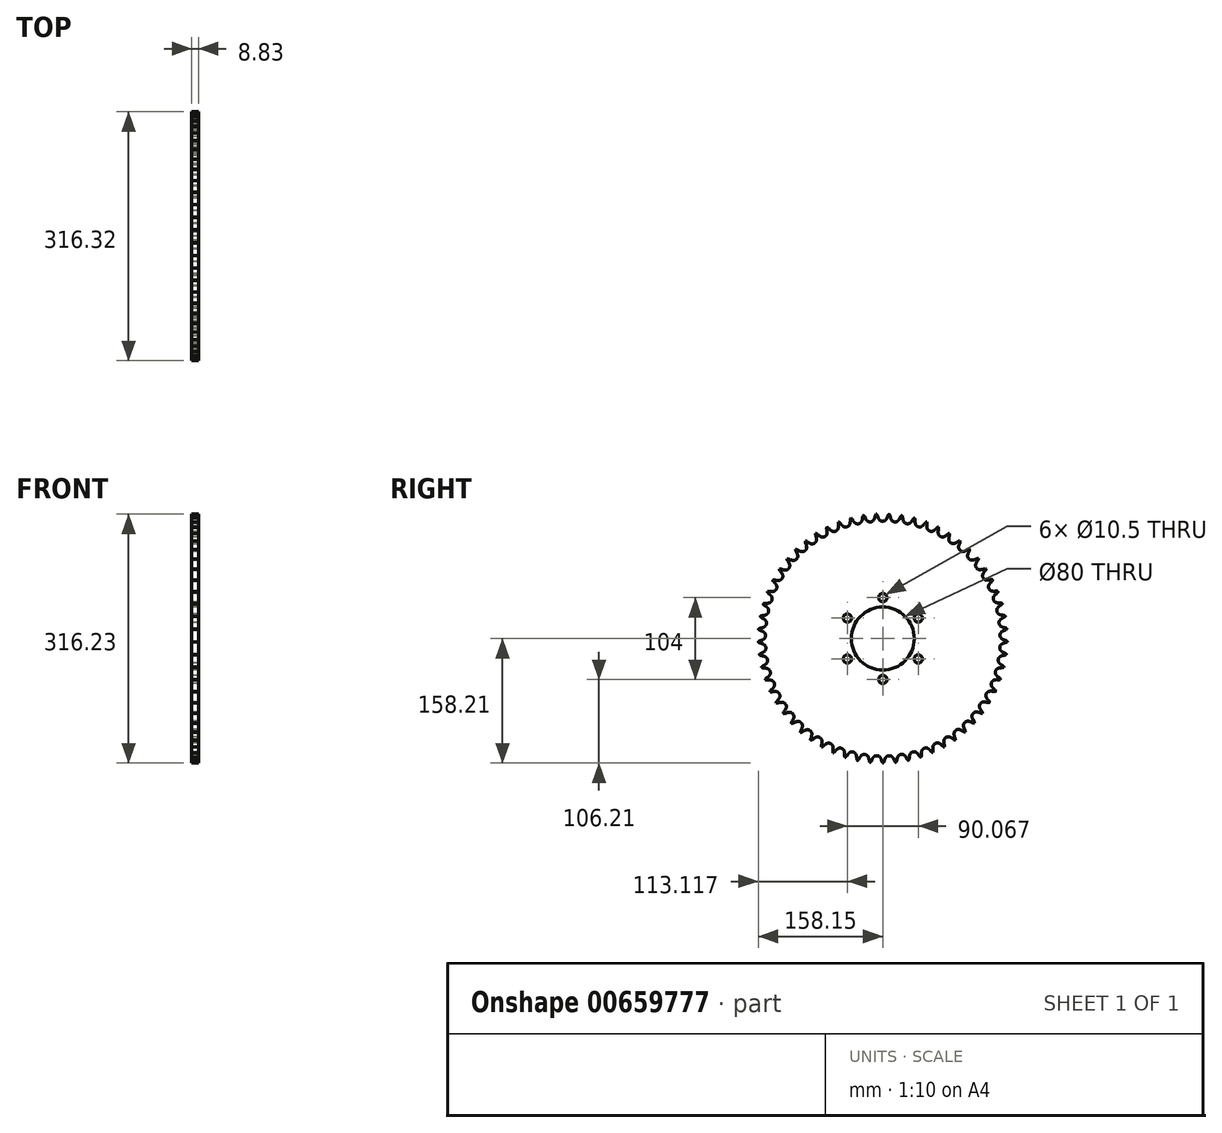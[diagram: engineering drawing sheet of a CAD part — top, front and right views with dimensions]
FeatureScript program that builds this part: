
annotation { "Feature Type Name" : "Feature", "Feature Type Description" : "" }
export const myFeature = defineFeature(function(context is Context, id is Id, definition is map)
    precondition{}
    {
        {
            var Q0;
            Q0=qCreatedBy(makeId("Front.planeOp"),FACE);
            var sketch = newSketch(context, id + "F0", { "sketchPlane" : qUnion([Q0])});
            skLineSegment(sketch, "E0", {"start": v(0, 0) * mm, "end": v(26.72, 0) * mm, "construction": true});
            skLineSegment(sketch, "E1.bottom", {"start": v(0, 40) * mm, "end": v(8.83, 40) * mm});
            skLineSegment(sketch, "E1.top", {"start": v(0, 158.2) * mm, "end": v(8.83, 158.2) * mm});
            skLineSegment(sketch, "E1.left", {"start": v(0, 40) * mm, "end": v(0, 158.2) * mm});
            skLineSegment(sketch, "E1.right", {"start": v(8.83, 40) * mm, "end": v(8.82, 158.2) * mm});
            skLineSegment(sketch, "E2.MirrorCS", {"start": v(8.83, -40) * mm, "end": v(8.83, -158.2) * mm});
            skLineSegment(sketch, "E3.MirrorCS", {"start": v(0, -158.2) * mm, "end": v(8.83, -158.2) * mm});
            skLineSegment(sketch, "E4.MirrorCS", {"start": v(0, -40) * mm, "end": v(8.83, -40) * mm});
            skLineSegment(sketch, "E5.MirrorCS", {"start": v(0, -40) * mm, "end": v(0, -158.2) * mm});
            skSolve(sketch);
        }
        {
            var Q0;
            Q0=makeQuery(id+"F0.imprint","IMPRINT",FACE,{"disambiguationData":[TD([[makeQuery(id+"F0.imprint","IMPRINT",EDGE,{"derivedFrom":sQuery(id+"F0.wireOp",EDGE,"E1.bottom")}),1.0]])]});
            var Q1;
            Q1=sQuery(id+"F0.wireOp",EDGE,"E0");
            revolve(context, id + "F1", {"entities" : qUnion([Q0]), "axis" : qUnion([Q1]), "revolveType" : RevolveType.FULL});
        }
        {
            var Q0;
            Q0=makeQuery(id+"F1.opRevolve","SWEPT_FACE",FACE,{"disambiguationData":[OSD([sQuery(id+"F0.wireOp",EDGE,"E1.left")])]});
            var sketch = newSketch(context, id + "F2", { "sketchPlane" : qUnion([Q0])});
            skCircle(sketch, "E6", {"center": v(0.24, 0) * mm, "radius": 158.2 * mm, "construction": true});
            skCircle(sketch, "E7", {"center": v(0.24, 0) * mm, "radius": 154.2 * mm, "construction": true});
            skCircle(sketch, "E8", {"center": v(0.24, 0) * mm, "radius": 149.03 * mm, "construction": true});
            skLineSegment(sketch, "E9", {"start": v(0.24, 0) * mm, "end": v(0.24, 107.73) * mm, "construction": true});
            skLineSegment(sketch, "E10", {"start": v(-4.24, 86.97) * mm, "end": v(0.24, 0) * mm, "construction": true});
            skLineSegment(sketch, "E11", {"start": v(0, 0) * mm, "end": v(0, 107.73) * mm, "construction": true});
            skLineSegment(sketch, "E12", {"start": v(0, 154.19) * mm, "end": v(-70.6, 102.92) * mm, "construction": true});
            skLineSegment(sketch, "E13", {"start": v(0, 154.19) * mm, "end": v(6.58, 158.97) * mm, "construction": true});
            skLineSegment(sketch, "E14", {"start": v(6.58, 158.97) * mm, "end": v(-48.08, 140.25) * mm, "construction": true});
            skLineSegment(sketch, "E15", {"start": v(-5.99, 154.66) * mm, "end": v(-6.34, 155.68) * mm});
            skLineSegment(sketch, "E16", {"start": v(-6.34, 155.68) * mm, "end": v(-12.58, 153.54) * mm, "construction": true});
            skArc(sketch, "E17", {"start": v(-5.99, 154.66) * mm, "mid": v(-5.21, 152.84) * mm, "end": v(-4.17, 151.16) * mm});
            skArc(sketch, "E18", {"start": v(-4.17, 151.16) * mm, "mid": v(18.37, 165.09) * mm, "end": v(-5.99, 154.66) * mm, "construction": true});
            skArc(sketch, "E19", {"start": v(0, 149.03) * mm, "mid": v(2.34, 158.78) * mm, "end": v(-4.17, 151.16) * mm, "construction": true});
            skArc(sketch, "E20", {"start": v(-4.17, 151.16) * mm, "mid": v(-2.34, 149.6) * mm, "end": v(0, 149.03) * mm});
            skLineSegment(sketch, "E21", {"start": v(0, 149.03) * mm, "end": v(0.24, 149.03) * mm});
            skArc(sketch, "E22", {"start": v(-7.92, 158.21) * mm, "mid": v(-18.18, 150.05) * mm, "end": v(-6.34, 155.68) * mm, "construction": true});
            skArc(sketch, "E23", {"start": v(-6.34, 155.68) * mm, "mid": v(-6.98, 157.04) * mm, "end": v(-7.92, 158.21) * mm});
            skArc(sketch, "E24.MirrorCS", {"start": v(4.65, 151.16) * mm, "mid": v(2.82, 149.6) * mm, "end": v(0.48, 149.03) * mm});
            skArc(sketch, "E25.MirrorCS", {"start": v(6.47, 154.66) * mm, "mid": v(5.69, 152.84) * mm, "end": v(4.65, 151.16) * mm});
            skLineSegment(sketch, "E26.MirrorCS", {"start": v(6.47, 154.66) * mm, "end": v(6.81, 155.68) * mm});
            skArc(sketch, "E27.MirrorCS", {"start": v(6.81, 155.68) * mm, "mid": v(7.46, 157.04) * mm, "end": v(8.4, 158.21) * mm});
            skLineSegment(sketch, "E28.MirrorCS", {"start": v(0.48, 149.03) * mm, "end": v(0.24, 149.03) * mm});
            skArc(sketch, "E29.1.0", {"start": v(-22.31, 154.2) * mm, "mid": v(-23.1, 155.49) * mm, "end": v(-24.14, 156.56) * mm});
            skArc(sketch, "E29.1.1", {"start": v(-9.23, 155.56) * mm, "mid": v(-8.73, 156.97) * mm, "end": v(-7.92, 158.23) * mm});
            skLineSegment(sketch, "E29.1.2", {"start": v(-9.47, 154.5) * mm, "end": v(-9.23, 155.56) * mm});
            skArc(sketch, "E29.1.3", {"start": v(-9.47, 154.5) * mm, "mid": v(-10.06, 152.62) * mm, "end": v(-10.92, 150.84) * mm});
            skArc(sketch, "E29.1.4", {"start": v(-10.92, 150.84) * mm, "mid": v(-12.58, 149.1) * mm, "end": v(-14.85, 148.3) * mm});
            skArc(sketch, "E29.1.5", {"start": v(-19.7, 149.93) * mm, "mid": v(-17.71, 148.56) * mm, "end": v(-15.32, 148.24) * mm});
            skArc(sketch, "E29.1.6", {"start": v(-21.86, 153.23) * mm, "mid": v(-20.9, 151.5) * mm, "end": v(-19.7, 149.93) * mm});
            skLineSegment(sketch, "E29.1.7", {"start": v(-21.86, 153.23) * mm, "end": v(-22.31, 154.2) * mm});
            skLineSegment(sketch, "E29.1.8", {"start": v(-14.85, 148.3) * mm, "end": v(-15.09, 148.27) * mm});
            skLineSegment(sketch, "E29.1.9", {"start": v(-15.32, 148.24) * mm, "end": v(-15.09, 148.27) * mm});
            skArc(sketch, "E29.2.0", {"start": v(-38.05, 151.1) * mm, "mid": v(-38.96, 152.29) * mm, "end": v(-40.11, 153.25) * mm});
            skArc(sketch, "E29.2.1", {"start": v(-25.17, 153.78) * mm, "mid": v(-24.82, 155.24) * mm, "end": v(-24.15, 156.58) * mm});
            skLineSegment(sketch, "E29.2.2", {"start": v(-25.3, 152.71) * mm, "end": v(-25.17, 153.78) * mm});
            skArc(sketch, "E29.2.3", {"start": v(-25.3, 152.71) * mm, "mid": v(-25.7, 150.78) * mm, "end": v(-26.37, 148.92) * mm});
            skArc(sketch, "E29.2.4", {"start": v(-26.37, 148.92) * mm, "mid": v(-27.84, 147.01) * mm, "end": v(-30.02, 145.98) * mm});
            skArc(sketch, "E29.2.5", {"start": v(-35, 147.11) * mm, "mid": v(-32.9, 145.96) * mm, "end": v(-30.49, 145.88) * mm});
            skArc(sketch, "E29.2.6", {"start": v(-37.5, 150.17) * mm, "mid": v(-36.37, 148.55) * mm, "end": v(-35, 147.11) * mm});
            skLineSegment(sketch, "E29.2.7", {"start": v(-37.5, 150.17) * mm, "end": v(-38.05, 151.1) * mm});
            skLineSegment(sketch, "E29.2.8", {"start": v(-30.02, 145.98) * mm, "end": v(-30.25, 145.93) * mm});
            skLineSegment(sketch, "E29.2.9", {"start": v(-30.49, 145.88) * mm, "end": v(-30.25, 145.93) * mm});
            skArc(sketch, "E29.3.0", {"start": v(-53.38, 146.38) * mm, "mid": v(-54.4, 147.47) * mm, "end": v(-55.66, 148.3) * mm});
            skArc(sketch, "E29.3.1", {"start": v(-40.85, 150.38) * mm, "mid": v(-40.65, 151.87) * mm, "end": v(-40.12, 153.27) * mm});
            skLineSegment(sketch, "E29.3.2", {"start": v(-40.88, 149.3) * mm, "end": v(-40.85, 150.38) * mm});
            skArc(sketch, "E29.3.3", {"start": v(-40.88, 149.3) * mm, "mid": v(-41.06, 147.33) * mm, "end": v(-41.54, 145.41) * mm});
            skArc(sketch, "E29.3.4", {"start": v(-41.54, 145.41) * mm, "mid": v(-42.81, 143.37) * mm, "end": v(-44.87, 142.12) * mm});
            skArc(sketch, "E29.3.5", {"start": v(-49.94, 142.73) * mm, "mid": v(-47.72, 141.8) * mm, "end": v(-45.32, 141.98) * mm});
            skArc(sketch, "E29.3.6", {"start": v(-52.74, 145.52) * mm, "mid": v(-51.45, 144.02) * mm, "end": v(-49.94, 142.73) * mm});
            skLineSegment(sketch, "E29.3.7", {"start": v(-52.74, 145.52) * mm, "end": v(-53.38, 146.38) * mm});
            skLineSegment(sketch, "E29.3.8", {"start": v(-44.87, 142.12) * mm, "end": v(-45.1, 142.05) * mm});
            skLineSegment(sketch, "E29.3.9", {"start": v(-45.32, 141.98) * mm, "end": v(-45.1, 142.05) * mm});
            skArc(sketch, "E29.4.0", {"start": v(-68.15, 140.11) * mm, "mid": v(-69.28, 141.1) * mm, "end": v(-70.61, 141.8) * mm});
            skArc(sketch, "E29.4.1", {"start": v(-56.1, 145.38) * mm, "mid": v(-56.05, 146.88) * mm, "end": v(-55.67, 148.33) * mm});
            skLineSegment(sketch, "E29.4.2", {"start": v(-56.01, 144.3) * mm, "end": v(-56.1, 145.38) * mm});
            skArc(sketch, "E29.4.3", {"start": v(-56.01, 144.3) * mm, "mid": v(-56, 142.33) * mm, "end": v(-56.27, 140.37) * mm});
            skArc(sketch, "E29.4.4", {"start": v(-56.27, 140.37) * mm, "mid": v(-57.33, 138.2) * mm, "end": v(-59.25, 136.75) * mm});
            skArc(sketch, "E29.4.5", {"start": v(-64.36, 136.84) * mm, "mid": v(-62.05, 136.14) * mm, "end": v(-59.68, 136.56) * mm});
            skArc(sketch, "E29.4.6", {"start": v(-67.42, 139.32) * mm, "mid": v(-65.98, 137.97) * mm, "end": v(-64.36, 136.84) * mm});
            skLineSegment(sketch, "E29.4.7", {"start": v(-67.42, 139.32) * mm, "end": v(-68.15, 140.11) * mm});
            skLineSegment(sketch, "E29.4.8", {"start": v(-59.25, 136.75) * mm, "end": v(-59.46, 136.66) * mm});
            skLineSegment(sketch, "E29.4.9", {"start": v(-59.68, 136.56) * mm, "end": v(-59.46, 136.66) * mm});
            skArc(sketch, "E29.5.0", {"start": v(-82.2, 132.36) * mm, "mid": v(-83.42, 133.23) * mm, "end": v(-84.82, 133.79) * mm});
            skArc(sketch, "E29.5.1", {"start": v(-70.75, 138.84) * mm, "mid": v(-70.86, 140.34) * mm, "end": v(-70.62, 141.82) * mm});
            skLineSegment(sketch, "E29.5.2", {"start": v(-70.55, 137.79) * mm, "end": v(-70.75, 138.84) * mm});
            skArc(sketch, "E29.5.3", {"start": v(-70.55, 137.79) * mm, "mid": v(-70.33, 135.82) * mm, "end": v(-70.4, 133.84) * mm});
            skArc(sketch, "E29.5.4", {"start": v(-70.4, 133.84) * mm, "mid": v(-71.23, 131.58) * mm, "end": v(-73, 129.94) * mm});
            skArc(sketch, "E29.5.5", {"start": v(-78.08, 129.5) * mm, "mid": v(-75.72, 129.04) * mm, "end": v(-73.4, 129.7) * mm});
            skArc(sketch, "E29.5.6", {"start": v(-81.4, 131.65) * mm, "mid": v(-79.82, 130.45) * mm, "end": v(-78.08, 129.5) * mm});
            skLineSegment(sketch, "E29.5.7", {"start": v(-81.4, 131.65) * mm, "end": v(-82.2, 132.36) * mm});
            skLineSegment(sketch, "E29.5.8", {"start": v(-73, 129.94) * mm, "end": v(-73.2, 129.82) * mm});
            skLineSegment(sketch, "E29.5.9", {"start": v(-73.4, 129.7) * mm, "end": v(-73.2, 129.82) * mm});
            skArc(sketch, "E29.6.0", {"start": v(-95.37, 123.21) * mm, "mid": v(-96.68, 123.94) * mm, "end": v(-98.12, 124.36) * mm});
            skArc(sketch, "E29.6.1", {"start": v(-84.65, 130.83) * mm, "mid": v(-84.91, 132.31) * mm, "end": v(-84.83, 133.8) * mm});
            skLineSegment(sketch, "E29.6.2", {"start": v(-84.35, 129.8) * mm, "end": v(-84.65, 130.83) * mm});
            skArc(sketch, "E29.6.3", {"start": v(-84.35, 129.8) * mm, "mid": v(-83.93, 127.87) * mm, "end": v(-83.8, 125.9) * mm});
            skArc(sketch, "E29.6.4", {"start": v(-83.8, 125.9) * mm, "mid": v(-84.38, 123.56) * mm, "end": v(-85.97, 121.74) * mm});
            skArc(sketch, "E29.6.5", {"start": v(-90.99, 120.78) * mm, "mid": v(-88.59, 120.57) * mm, "end": v(-86.35, 121.47) * mm});
            skArc(sketch, "E29.6.6", {"start": v(-94.5, 122.58) * mm, "mid": v(-92.8, 121.55) * mm, "end": v(-90.99, 120.78) * mm});
            skLineSegment(sketch, "E29.6.7", {"start": v(-94.5, 122.58) * mm, "end": v(-95.37, 123.21) * mm});
            skLineSegment(sketch, "E29.6.8", {"start": v(-85.97, 121.74) * mm, "end": v(-86.16, 121.6) * mm});
            skLineSegment(sketch, "E29.6.9", {"start": v(-86.35, 121.47) * mm, "end": v(-86.16, 121.6) * mm});
            skArc(sketch, "E29.7.0", {"start": v(-107.53, 112.75) * mm, "mid": v(-108.91, 113.34) * mm, "end": v(-110.39, 113.61) * mm});
            skArc(sketch, "E29.7.1", {"start": v(-97.65, 121.43) * mm, "mid": v(-98.06, 122.88) * mm, "end": v(-98.14, 124.38) * mm});
            skLineSegment(sketch, "E29.7.2", {"start": v(-97.24, 120.44) * mm, "end": v(-97.65, 121.43) * mm});
            skArc(sketch, "E29.7.3", {"start": v(-97.24, 120.44) * mm, "mid": v(-96.63, 118.56) * mm, "end": v(-96.3, 116.6) * mm});
            skArc(sketch, "E29.7.4", {"start": v(-96.3, 116.6) * mm, "mid": v(-96.64, 114.23) * mm, "end": v(-98.03, 112.26) * mm});
            skArc(sketch, "E29.7.5", {"start": v(-102.92, 110.79) * mm, "mid": v(-100.52, 110.82) * mm, "end": v(-98.39, 111.94) * mm});
            skArc(sketch, "E29.7.6", {"start": v(-106.6, 112.22) * mm, "mid": v(-104.81, 111.37) * mm, "end": v(-102.92, 110.79) * mm});
            skLineSegment(sketch, "E29.7.7", {"start": v(-106.6, 112.22) * mm, "end": v(-107.53, 112.75) * mm});
            skLineSegment(sketch, "E29.7.8", {"start": v(-98.03, 112.26) * mm, "end": v(-98.2, 112.1) * mm});
            skLineSegment(sketch, "E29.7.9", {"start": v(-98.39, 111.94) * mm, "end": v(-98.2, 112.1) * mm});
            skArc(sketch, "E29.8.0", {"start": v(-118.56, 101.1) * mm, "mid": v(-119.99, 101.55) * mm, "end": v(-121.49, 101.66) * mm});
            skArc(sketch, "E29.8.1", {"start": v(-109.62, 110.75) * mm, "mid": v(-110.18, 112.14) * mm, "end": v(-110.4, 113.63) * mm});
            skLineSegment(sketch, "E29.8.2", {"start": v(-109.11, 109.8) * mm, "end": v(-109.62, 110.75) * mm});
            skArc(sketch, "E29.8.3", {"start": v(-109.11, 109.8) * mm, "mid": v(-108.3, 108) * mm, "end": v(-107.78, 106.1) * mm});
            skArc(sketch, "E29.8.4", {"start": v(-107.78, 106.1) * mm, "mid": v(-107.87, 103.68) * mm, "end": v(-109.05, 101.58) * mm});
            skArc(sketch, "E29.8.5", {"start": v(-113.77, 99.62) * mm, "mid": v(-111.38, 99.9) * mm, "end": v(-109.37, 101.24) * mm});
            skArc(sketch, "E29.8.6", {"start": v(-117.57, 100.66) * mm, "mid": v(-115.7, 100) * mm, "end": v(-113.77, 99.62) * mm});
            skLineSegment(sketch, "E29.8.7", {"start": v(-117.57, 100.66) * mm, "end": v(-118.56, 101.1) * mm});
            skLineSegment(sketch, "E29.8.8", {"start": v(-109.05, 101.58) * mm, "end": v(-109.21, 101.41) * mm});
            skLineSegment(sketch, "E29.8.9", {"start": v(-109.37, 101.24) * mm, "end": v(-109.21, 101.41) * mm});
            skArc(sketch, "E29.9.0", {"start": v(-128.32, 88.37) * mm, "mid": v(-129.8, 88.67) * mm, "end": v(-131.3, 88.63) * mm});
            skArc(sketch, "E29.9.1", {"start": v(-120.43, 98.9) * mm, "mid": v(-121.13, 100.22) * mm, "end": v(-121.5, 101.67) * mm});
            skLineSegment(sketch, "E29.9.2", {"start": v(-119.82, 98) * mm, "end": v(-120.43, 98.9) * mm});
            skArc(sketch, "E29.9.3", {"start": v(-119.82, 98) * mm, "mid": v(-118.84, 96.29) * mm, "end": v(-118.12, 94.45) * mm});
            skArc(sketch, "E29.9.4", {"start": v(-118.12, 94.45) * mm, "mid": v(-117.96, 92.04) * mm, "end": v(-118.92, 89.83) * mm});
            skArc(sketch, "E29.9.5", {"start": v(-123.4, 87.4) * mm, "mid": v(-121.06, 87.92) * mm, "end": v(-119.2, 89.45) * mm});
            skArc(sketch, "E29.9.6", {"start": v(-127.3, 88.04) * mm, "mid": v(-125.38, 87.57) * mm, "end": v(-123.4, 87.4) * mm});
            skLineSegment(sketch, "E29.9.7", {"start": v(-127.3, 88.04) * mm, "end": v(-128.32, 88.37) * mm});
            skLineSegment(sketch, "E29.9.8", {"start": v(-118.92, 89.83) * mm, "end": v(-119.06, 89.64) * mm});
            skLineSegment(sketch, "E29.9.9", {"start": v(-119.2, 89.45) * mm, "end": v(-119.06, 89.64) * mm});
            skArc(sketch, "E29.10.0", {"start": v(-136.73, 74.7) * mm, "mid": v(-138.22, 74.85) * mm, "end": v(-139.71, 74.66) * mm});
            skArc(sketch, "E29.10.1", {"start": v(-129.96, 85.98) * mm, "mid": v(-130.79, 87.24) * mm, "end": v(-131.32, 88.64) * mm});
            skLineSegment(sketch, "E29.10.2", {"start": v(-129.27, 85.16) * mm, "end": v(-129.96, 85.98) * mm});
            skArc(sketch, "E29.10.3", {"start": v(-129.27, 85.16) * mm, "mid": v(-128.1, 83.56) * mm, "end": v(-127.2, 81.8) * mm});
            skArc(sketch, "E29.10.4", {"start": v(-127.2, 81.8) * mm, "mid": v(-126.8, 79.43) * mm, "end": v(-127.52, 77.13) * mm});
            skArc(sketch, "E29.10.5", {"start": v(-131.74, 74.24) * mm, "mid": v(-129.46, 75) * mm, "end": v(-127.77, 76.72) * mm});
            skArc(sketch, "E29.10.6", {"start": v(-135.68, 74.48) * mm, "mid": v(-133.72, 74.22) * mm, "end": v(-131.74, 74.24) * mm});
            skLineSegment(sketch, "E29.10.7", {"start": v(-135.68, 74.48) * mm, "end": v(-136.73, 74.7) * mm});
            skLineSegment(sketch, "E29.10.8", {"start": v(-127.52, 77.13) * mm, "end": v(-127.65, 76.93) * mm});
            skLineSegment(sketch, "E29.10.9", {"start": v(-127.77, 76.72) * mm, "end": v(-127.65, 76.93) * mm});
            skArc(sketch, "E29.11.0", {"start": v(-143.69, 60.25) * mm, "mid": v(-145.19, 60.25) * mm, "end": v(-146.65, 59.9) * mm});
            skArc(sketch, "E29.11.1", {"start": v(-138.11, 72.17) * mm, "mid": v(-139.07, 73.32) * mm, "end": v(-139.73, 74.67) * mm});
            skLineSegment(sketch, "E29.11.2", {"start": v(-137.34, 71.42) * mm, "end": v(-138.11, 72.17) * mm});
            skArc(sketch, "E29.11.3", {"start": v(-137.34, 71.42) * mm, "mid": v(-136.02, 69.94) * mm, "end": v(-134.94, 68.29) * mm});
            skArc(sketch, "E29.11.4", {"start": v(-134.94, 68.29) * mm, "mid": v(-134.3, 65.97) * mm, "end": v(-134.78, 63.6) * mm});
            skArc(sketch, "E29.11.5", {"start": v(-138.68, 60.3) * mm, "mid": v(-136.48, 61.3) * mm, "end": v(-134.98, 63.18) * mm});
            skArc(sketch, "E29.11.6", {"start": v(-142.62, 60.14) * mm, "mid": v(-140.64, 60.07) * mm, "end": v(-138.68, 60.3) * mm});
            skLineSegment(sketch, "E29.11.7", {"start": v(-142.62, 60.14) * mm, "end": v(-143.69, 60.25) * mm});
            skLineSegment(sketch, "E29.11.8", {"start": v(-134.78, 63.6) * mm, "end": v(-134.88, 63.4) * mm});
            skLineSegment(sketch, "E29.11.9", {"start": v(-134.98, 63.18) * mm, "end": v(-134.88, 63.4) * mm});
            skArc(sketch, "E29.12.0", {"start": v(-149.12, 45.16) * mm, "mid": v(-150.61, 45) * mm, "end": v(-152.03, 44.5) * mm});
            skArc(sketch, "E29.12.1", {"start": v(-144.8, 57.58) * mm, "mid": v(-145.87, 58.64) * mm, "end": v(-146.67, 59.9) * mm});
            skLineSegment(sketch, "E29.12.2", {"start": v(-143.95, 56.92) * mm, "end": v(-144.8, 57.58) * mm});
            skArc(sketch, "E29.12.3", {"start": v(-143.95, 56.92) * mm, "mid": v(-142.5, 55.59) * mm, "end": v(-141.24, 54.05) * mm});
            skArc(sketch, "E29.12.4", {"start": v(-141.24, 54.05) * mm, "mid": v(-140.37, 51.8) * mm, "end": v(-140.6, 49.41) * mm});
            skArc(sketch, "E29.12.5", {"start": v(-144.14, 45.72) * mm, "mid": v(-142.06, 46.94) * mm, "end": v(-140.76, 48.96) * mm});
            skArc(sketch, "E29.12.6", {"start": v(-148.04, 45.16) * mm, "mid": v(-146.07, 45.3) * mm, "end": v(-144.14, 45.72) * mm});
            skLineSegment(sketch, "E29.12.7", {"start": v(-148.04, 45.16) * mm, "end": v(-149.12, 45.16) * mm});
            skLineSegment(sketch, "E29.12.8", {"start": v(-140.6, 49.41) * mm, "end": v(-140.68, 49.19) * mm});
            skLineSegment(sketch, "E29.12.9", {"start": v(-140.76, 48.96) * mm, "end": v(-140.68, 49.19) * mm});
            skArc(sketch, "E29.13.0", {"start": v(-152.97, 29.59) * mm, "mid": v(-154.44, 29.27) * mm, "end": v(-155.8, 28.63) * mm});
            skArc(sketch, "E29.13.1", {"start": v(-149.95, 42.39) * mm, "mid": v(-151.12, 43.33) * mm, "end": v(-152.05, 44.5) * mm});
            skLineSegment(sketch, "E29.13.2", {"start": v(-149.04, 41.82) * mm, "end": v(-149.95, 42.39) * mm});
            skArc(sketch, "E29.13.3", {"start": v(-149.04, 41.82) * mm, "mid": v(-147.45, 40.64) * mm, "end": v(-146.05, 39.24) * mm});
            skArc(sketch, "E29.13.4", {"start": v(-146.05, 39.24) * mm, "mid": v(-144.95, 37.1) * mm, "end": v(-144.94, 34.7) * mm});
            skArc(sketch, "E29.13.5", {"start": v(-148.08, 30.66) * mm, "mid": v(-146.14, 32.08) * mm, "end": v(-145.05, 34.23) * mm});
            skArc(sketch, "E29.13.6", {"start": v(-151.9, 29.7) * mm, "mid": v(-149.95, 30.03) * mm, "end": v(-148.08, 30.66) * mm});
            skLineSegment(sketch, "E29.13.7", {"start": v(-151.9, 29.7) * mm, "end": v(-152.97, 29.59) * mm});
            skLineSegment(sketch, "E29.13.8", {"start": v(-144.94, 34.7) * mm, "end": v(-145, 34.46) * mm});
            skLineSegment(sketch, "E29.13.9", {"start": v(-145.05, 34.23) * mm, "end": v(-145, 34.46) * mm});
            skArc(sketch, "E29.14.0", {"start": v(-155.2, 13.7) * mm, "mid": v(-156.63, 13.24) * mm, "end": v(-157.92, 12.46) * mm});
            skArc(sketch, "E29.14.1", {"start": v(-153.52, 26.75) * mm, "mid": v(-154.78, 27.56) * mm, "end": v(-155.82, 28.64) * mm});
            skLineSegment(sketch, "E29.14.2", {"start": v(-152.55, 26.27) * mm, "end": v(-153.52, 26.75) * mm});
            skArc(sketch, "E29.14.3", {"start": v(-152.55, 26.27) * mm, "mid": v(-150.85, 25.27) * mm, "end": v(-149.31, 24.02) * mm});
            skArc(sketch, "E29.14.4", {"start": v(-149.31, 24.02) * mm, "mid": v(-148, 22) * mm, "end": v(-147.74, 19.6) * mm});
            skArc(sketch, "E29.14.5", {"start": v(-150.45, 15.27) * mm, "mid": v(-148.66, 16.89) * mm, "end": v(-147.8, 19.14) * mm});
            skArc(sketch, "E29.14.6", {"start": v(-154.15, 13.92) * mm, "mid": v(-152.25, 14.46) * mm, "end": v(-150.45, 15.27) * mm});
            skLineSegment(sketch, "E29.14.7", {"start": v(-154.15, 13.92) * mm, "end": v(-155.2, 13.7) * mm});
            skLineSegment(sketch, "E29.14.8", {"start": v(-147.74, 19.6) * mm, "end": v(-147.77, 19.37) * mm});
            skLineSegment(sketch, "E29.14.9", {"start": v(-147.8, 19.14) * mm, "end": v(-147.77, 19.37) * mm});
            skArc(sketch, "E29.15.0", {"start": v(-155.8, -2.33) * mm, "mid": v(-157.16, -2.94) * mm, "end": v(-158.36, -3.84) * mm});
            skArc(sketch, "E29.15.1", {"start": v(-155.45, 10.82) * mm, "mid": v(-156.8, 11.5) * mm, "end": v(-157.94, 12.46) * mm});
            skLineSegment(sketch, "E29.15.2", {"start": v(-154.44, 10.45) * mm, "end": v(-155.45, 10.82) * mm});
            skArc(sketch, "E29.15.3", {"start": v(-154.44, 10.45) * mm, "mid": v(-152.65, 9.62) * mm, "end": v(-151, 8.54) * mm});
            skArc(sketch, "E29.15.4", {"start": v(-151, 8.54) * mm, "mid": v(-149.47, 6.67) * mm, "end": v(-148.97, 4.31) * mm});
            skArc(sketch, "E29.15.5", {"start": v(-151.22, -0.28) * mm, "mid": v(-149.6, 1.51) * mm, "end": v(-148.99, 3.84) * mm});
            skArc(sketch, "E29.15.6", {"start": v(-154.77, -2) * mm, "mid": v(-152.93, -1.27) * mm, "end": v(-151.22, -0.28) * mm});
            skLineSegment(sketch, "E29.15.7", {"start": v(-154.77, -2) * mm, "end": v(-155.8, -2.33) * mm});
            skLineSegment(sketch, "E29.15.8", {"start": v(-148.97, 4.31) * mm, "end": v(-148.98, 4.08) * mm});
            skLineSegment(sketch, "E29.15.9", {"start": v(-148.99, 3.84) * mm, "end": v(-148.98, 4.08) * mm});
            skArc(sketch, "E29.16.0", {"start": v(-154.73, -18.33) * mm, "mid": v(-156.03, -19.08) * mm, "end": v(-157.13, -20.1) * mm});
            skArc(sketch, "E29.16.1", {"start": v(-155.74, -5.22) * mm, "mid": v(-157.14, -4.68) * mm, "end": v(-158.39, -3.84) * mm});
            skLineSegment(sketch, "E29.16.2", {"start": v(-154.7, -5.49) * mm, "end": v(-155.74, -5.22) * mm});
            skArc(sketch, "E29.16.3", {"start": v(-154.7, -5.49) * mm, "mid": v(-152.83, -6.13) * mm, "end": v(-151.07, -7.03) * mm});
            skArc(sketch, "E29.16.4", {"start": v(-151.07, -7.03) * mm, "mid": v(-149.37, -8.74) * mm, "end": v(-148.63, -11.03) * mm});
            skArc(sketch, "E29.16.5", {"start": v(-150.39, -15.82) * mm, "mid": v(-148.97, -13.88) * mm, "end": v(-148.6, -11.5) * mm});
            skArc(sketch, "E29.16.6", {"start": v(-153.74, -17.9) * mm, "mid": v(-151.99, -17) * mm, "end": v(-150.39, -15.82) * mm});
            skLineSegment(sketch, "E29.16.7", {"start": v(-153.74, -17.9) * mm, "end": v(-154.73, -18.33) * mm});
            skLineSegment(sketch, "E29.16.8", {"start": v(-148.63, -11.03) * mm, "end": v(-148.6, -11.26) * mm});
            skLineSegment(sketch, "E29.16.9", {"start": v(-148.6, -11.5) * mm, "end": v(-148.6, -11.26) * mm});
            skArc(sketch, "E29.17.0", {"start": v(-152.02, -34.15) * mm, "mid": v(-153.24, -35.02) * mm, "end": v(-154.23, -36.15) * mm});
            skArc(sketch, "E29.17.1", {"start": v(-154.38, -21.2) * mm, "mid": v(-155.83, -20.82) * mm, "end": v(-157.15, -20.1) * mm});
            skLineSegment(sketch, "E29.17.2", {"start": v(-153.32, -21.37) * mm, "end": v(-154.38, -21.2) * mm});
            skArc(sketch, "E29.17.3", {"start": v(-153.32, -21.37) * mm, "mid": v(-151.39, -21.8) * mm, "end": v(-149.55, -22.53) * mm});
            skArc(sketch, "E29.17.4", {"start": v(-149.55, -22.53) * mm, "mid": v(-147.68, -24.05) * mm, "end": v(-146.7, -26.25) * mm});
            skArc(sketch, "E29.17.5", {"start": v(-147.96, -31.2) * mm, "mid": v(-146.75, -29.12) * mm, "end": v(-146.62, -26.72) * mm});
            skArc(sketch, "E29.17.6", {"start": v(-151.08, -33.62) * mm, "mid": v(-149.43, -32.53) * mm, "end": v(-147.96, -31.2) * mm});
            skLineSegment(sketch, "E29.17.7", {"start": v(-151.08, -33.62) * mm, "end": v(-152.02, -34.15) * mm});
            skLineSegment(sketch, "E29.17.8", {"start": v(-146.7, -26.25) * mm, "end": v(-146.66, -26.48) * mm});
            skLineSegment(sketch, "E29.17.9", {"start": v(-146.62, -26.72) * mm, "end": v(-146.66, -26.48) * mm});
            skArc(sketch, "E29.18.0", {"start": v(-147.7, -49.6) * mm, "mid": v(-148.83, -50.6) * mm, "end": v(-149.7, -51.82) * mm});
            skArc(sketch, "E29.18.1", {"start": v(-151.38, -36.97) * mm, "mid": v(-152.86, -36.73) * mm, "end": v(-154.25, -36.16) * mm});
            skLineSegment(sketch, "E29.18.2", {"start": v(-150.3, -37.02) * mm, "end": v(-151.38, -36.97) * mm});
            skArc(sketch, "E29.18.3", {"start": v(-150.3, -37.02) * mm, "mid": v(-148.34, -37.26) * mm, "end": v(-146.44, -37.79) * mm});
            skArc(sketch, "E29.18.4", {"start": v(-146.44, -37.79) * mm, "mid": v(-144.42, -39.1) * mm, "end": v(-143.23, -41.2) * mm});
            skArc(sketch, "E29.18.5", {"start": v(-143.97, -46.25) * mm, "mid": v(-142.98, -44.06) * mm, "end": v(-143.1, -41.65) * mm});
            skArc(sketch, "E29.18.6", {"start": v(-146.83, -48.98) * mm, "mid": v(-145.3, -47.72) * mm, "end": v(-143.97, -46.25) * mm});
            skLineSegment(sketch, "E29.18.7", {"start": v(-146.83, -48.98) * mm, "end": v(-147.7, -49.6) * mm});
            skLineSegment(sketch, "E29.18.8", {"start": v(-143.23, -41.2) * mm, "end": v(-143.16, -41.42) * mm});
            skLineSegment(sketch, "E29.18.9", {"start": v(-143.1, -41.65) * mm, "end": v(-143.16, -41.42) * mm});
            skArc(sketch, "E29.19.0", {"start": v(-141.82, -64.52) * mm, "mid": v(-142.84, -65.63) * mm, "end": v(-143.57, -66.94) * mm});
            skArc(sketch, "E29.19.1", {"start": v(-146.78, -52.34) * mm, "mid": v(-148.28, -52.25) * mm, "end": v(-149.72, -51.83) * mm});
            skLineSegment(sketch, "E29.19.2", {"start": v(-145.7, -52.28) * mm, "end": v(-146.78, -52.34) * mm});
            skArc(sketch, "E29.19.3", {"start": v(-145.7, -52.28) * mm, "mid": v(-143.73, -52.31) * mm, "end": v(-141.77, -52.64) * mm});
            skArc(sketch, "E29.19.4", {"start": v(-141.77, -52.64) * mm, "mid": v(-139.64, -53.75) * mm, "end": v(-138.23, -55.7) * mm});
            skArc(sketch, "E29.19.5", {"start": v(-138.45, -60.81) * mm, "mid": v(-137.7, -58.53) * mm, "end": v(-138.05, -56.15) * mm});
            skArc(sketch, "E29.19.6", {"start": v(-141.01, -63.81) * mm, "mid": v(-139.62, -62.4) * mm, "end": v(-138.45, -60.81) * mm});
            skLineSegment(sketch, "E29.19.7", {"start": v(-141.01, -63.81) * mm, "end": v(-141.82, -64.52) * mm});
            skLineSegment(sketch, "E29.19.8", {"start": v(-138.23, -55.7) * mm, "end": v(-138.14, -55.93) * mm});
            skLineSegment(sketch, "E29.19.9", {"start": v(-138.05, -56.15) * mm, "end": v(-138.14, -55.93) * mm});
            skArc(sketch, "E29.20.0", {"start": v(-134.44, -78.76) * mm, "mid": v(-135.33, -79.97) * mm, "end": v(-135.93, -81.34) * mm});
            skArc(sketch, "E29.20.1", {"start": v(-140.62, -67.15) * mm, "mid": v(-142.12, -67.22) * mm, "end": v(-143.6, -66.95) * mm});
            skLineSegment(sketch, "E29.20.2", {"start": v(-139.56, -66.98) * mm, "end": v(-140.62, -67.15) * mm});
            skArc(sketch, "E29.20.3", {"start": v(-139.56, -66.98) * mm, "mid": v(-137.58, -66.81) * mm, "end": v(-135.61, -66.94) * mm});
            skArc(sketch, "E29.20.4", {"start": v(-135.61, -66.94) * mm, "mid": v(-133.37, -67.82) * mm, "end": v(-131.77, -69.62) * mm});
            skArc(sketch, "E29.20.5", {"start": v(-131.47, -74.72) * mm, "mid": v(-130.95, -72.37) * mm, "end": v(-131.55, -70.04) * mm});
            skArc(sketch, "E29.20.6", {"start": v(-133.7, -77.97) * mm, "mid": v(-132.46, -76.43) * mm, "end": v(-131.47, -74.72) * mm});
            skLineSegment(sketch, "E29.20.7", {"start": v(-133.7, -77.97) * mm, "end": v(-134.44, -78.76) * mm});
            skLineSegment(sketch, "E29.20.8", {"start": v(-131.77, -69.62) * mm, "end": v(-131.66, -69.83) * mm});
            skLineSegment(sketch, "E29.20.9", {"start": v(-131.55, -70.04) * mm, "end": v(-131.66, -69.83) * mm});
            skArc(sketch, "E29.21.0", {"start": v(-125.63, -92.17) * mm, "mid": v(-126.4, -93.46) * mm, "end": v(-126.84, -94.89) * mm});
            skArc(sketch, "E29.21.1", {"start": v(-132.97, -81.25) * mm, "mid": v(-134.45, -81.48) * mm, "end": v(-135.95, -81.36) * mm});
            skLineSegment(sketch, "E29.21.2", {"start": v(-131.93, -80.97) * mm, "end": v(-132.97, -81.25) * mm});
            skArc(sketch, "E29.21.3", {"start": v(-131.93, -80.97) * mm, "mid": v(-129.99, -80.6) * mm, "end": v(-128, -80.53) * mm});
            skArc(sketch, "E29.21.4", {"start": v(-128, -80.53) * mm, "mid": v(-125.69, -81.17) * mm, "end": v(-123.92, -82.8) * mm});
            skArc(sketch, "E29.21.5", {"start": v(-123.09, -87.85) * mm, "mid": v(-122.81, -85.45) * mm, "end": v(-123.65, -83.2) * mm});
            skArc(sketch, "E29.21.6", {"start": v(-124.98, -91.3) * mm, "mid": v(-123.9, -89.65) * mm, "end": v(-123.09, -87.85) * mm});
            skLineSegment(sketch, "E29.21.7", {"start": v(-124.98, -91.3) * mm, "end": v(-125.63, -92.17) * mm});
            skLineSegment(sketch, "E29.21.8", {"start": v(-123.92, -82.8) * mm, "end": v(-123.78, -83) * mm});
            skLineSegment(sketch, "E29.21.9", {"start": v(-123.65, -83.2) * mm, "end": v(-123.78, -83) * mm});
            skArc(sketch, "E29.22.0", {"start": v(-115.48, -104.6) * mm, "mid": v(-116.11, -105.96) * mm, "end": v(-116.41, -107.43) * mm});
            skArc(sketch, "E29.22.1", {"start": v(-123.9, -94.5) * mm, "mid": v(-125.36, -94.87) * mm, "end": v(-126.86, -94.9) * mm});
            skLineSegment(sketch, "E29.22.2", {"start": v(-122.9, -94.11) * mm, "end": v(-123.9, -94.5) * mm});
            skArc(sketch, "E29.22.3", {"start": v(-122.9, -94.11) * mm, "mid": v(-121, -93.54) * mm, "end": v(-119.05, -93.26) * mm});
            skArc(sketch, "E29.22.4", {"start": v(-119.05, -93.26) * mm, "mid": v(-116.68, -93.67) * mm, "end": v(-114.75, -95.1) * mm});
            skArc(sketch, "E29.22.5", {"start": v(-113.4, -100.04) * mm, "mid": v(-113.37, -97.63) * mm, "end": v(-114.44, -95.47) * mm});
            skArc(sketch, "E29.22.6", {"start": v(-114.93, -103.68) * mm, "mid": v(-114.03, -101.91) * mm, "end": v(-113.4, -100.04) * mm});
            skLineSegment(sketch, "E29.22.7", {"start": v(-114.93, -103.68) * mm, "end": v(-115.48, -104.6) * mm});
            skLineSegment(sketch, "E29.22.8", {"start": v(-114.75, -95.1) * mm, "end": v(-114.6, -95.29) * mm});
            skLineSegment(sketch, "E29.22.9", {"start": v(-114.44, -95.47) * mm, "end": v(-114.6, -95.29) * mm});
            skArc(sketch, "E29.23.0", {"start": v(-104.12, -115.91) * mm, "mid": v(-104.6, -117.33) * mm, "end": v(-104.75, -118.83) * mm});
            skArc(sketch, "E29.23.1", {"start": v(-113.54, -106.73) * mm, "mid": v(-114.94, -107.26) * mm, "end": v(-116.43, -107.44) * mm});
            skLineSegment(sketch, "E29.23.2", {"start": v(-112.58, -106.25) * mm, "end": v(-113.54, -106.73) * mm});
            skArc(sketch, "E29.23.3", {"start": v(-112.58, -106.25) * mm, "mid": v(-110.75, -105.5) * mm, "end": v(-108.83, -105.01) * mm});
            skArc(sketch, "E29.23.4", {"start": v(-108.83, -105.01) * mm, "mid": v(-106.43, -105.17) * mm, "end": v(-104.36, -106.4) * mm});
            skArc(sketch, "E29.23.5", {"start": v(-102.51, -111.17) * mm, "mid": v(-102.73, -108.77) * mm, "end": v(-104.02, -106.73) * mm});
            skArc(sketch, "E29.23.6", {"start": v(-103.66, -114.94) * mm, "mid": v(-102.94, -113.1) * mm, "end": v(-102.51, -111.17) * mm});
            skLineSegment(sketch, "E29.23.7", {"start": v(-103.66, -114.94) * mm, "end": v(-104.12, -115.91) * mm});
            skLineSegment(sketch, "E29.23.8", {"start": v(-104.36, -106.4) * mm, "end": v(-104.19, -106.57) * mm});
            skLineSegment(sketch, "E29.23.9", {"start": v(-104.02, -106.73) * mm, "end": v(-104.19, -106.57) * mm});
            skArc(sketch, "E29.24.0", {"start": v(-91.65, -126) * mm, "mid": v(-91.98, -127.47) * mm, "end": v(-91.98, -128.97) * mm});
            skArc(sketch, "E29.24.1", {"start": v(-101.96, -117.84) * mm, "mid": v(-103.3, -118.5) * mm, "end": v(-104.77, -118.85) * mm});
            skLineSegment(sketch, "E29.24.2", {"start": v(-101.05, -117.26) * mm, "end": v(-101.96, -117.84) * mm});
            skArc(sketch, "E29.24.3", {"start": v(-101.05, -117.26) * mm, "mid": v(-99.32, -116.32) * mm, "end": v(-97.46, -115.64) * mm});
            skArc(sketch, "E29.24.4", {"start": v(-97.46, -115.64) * mm, "mid": v(-95.05, -115.55) * mm, "end": v(-92.87, -116.57) * mm});
            skArc(sketch, "E29.24.5", {"start": v(-90.54, -121.12) * mm, "mid": v(-91, -118.75) * mm, "end": v(-92.5, -116.86) * mm});
            skArc(sketch, "E29.24.6", {"start": v(-91.29, -125) * mm, "mid": v(-90.77, -123.08) * mm, "end": v(-90.54, -121.12) * mm});
            skLineSegment(sketch, "E29.24.7", {"start": v(-91.29, -125) * mm, "end": v(-91.65, -126) * mm});
            skLineSegment(sketch, "E29.24.8", {"start": v(-92.87, -116.57) * mm, "end": v(-92.68, -116.71) * mm});
            skLineSegment(sketch, "E29.24.9", {"start": v(-92.5, -116.86) * mm, "end": v(-92.68, -116.71) * mm});
            skArc(sketch, "E29.25.0", {"start": v(-78.2, -134.76) * mm, "mid": v(-78.39, -136.25) * mm, "end": v(-78.23, -137.74) * mm});
            skArc(sketch, "E29.25.1", {"start": v(-89.3, -127.7) * mm, "mid": v(-90.57, -128.5) * mm, "end": v(-92, -128.99) * mm});
            skLineSegment(sketch, "E29.25.2", {"start": v(-88.46, -127.03) * mm, "end": v(-89.3, -127.7) * mm});
            skArc(sketch, "E29.25.3", {"start": v(-88.46, -127.03) * mm, "mid": v(-86.83, -125.91) * mm, "end": v(-85.05, -125.05) * mm});
            skArc(sketch, "E29.25.4", {"start": v(-85.05, -125.05) * mm, "mid": v(-82.67, -124.71) * mm, "end": v(-80.39, -125.5) * mm});
            skArc(sketch, "E29.25.5", {"start": v(-77.6, -129.78) * mm, "mid": v(-78.31, -127.48) * mm, "end": v(-79.99, -125.75) * mm});
            skArc(sketch, "E29.25.6", {"start": v(-77.95, -133.72) * mm, "mid": v(-77.63, -131.76) * mm, "end": v(-77.6, -129.78) * mm});
            skLineSegment(sketch, "E29.25.7", {"start": v(-77.95, -133.72) * mm, "end": v(-78.2, -134.76) * mm});
            skLineSegment(sketch, "E29.25.8", {"start": v(-80.39, -125.5) * mm, "end": v(-80.19, -125.62) * mm});
            skLineSegment(sketch, "E29.25.9", {"start": v(-79.99, -125.75) * mm, "end": v(-80.19, -125.62) * mm});
            skArc(sketch, "E29.26.0", {"start": v(-63.93, -142.09) * mm, "mid": v(-63.96, -143.59) * mm, "end": v(-63.65, -145.06) * mm});
            skArc(sketch, "E29.26.1", {"start": v(-75.7, -136.2) * mm, "mid": v(-76.88, -137.13) * mm, "end": v(-78.24, -137.76) * mm});
            skLineSegment(sketch, "E29.26.2", {"start": v(-74.93, -135.45) * mm, "end": v(-75.7, -136.2) * mm});
            skArc(sketch, "E29.26.3", {"start": v(-74.93, -135.45) * mm, "mid": v(-73.42, -134.17) * mm, "end": v(-71.74, -133.13) * mm});
            skArc(sketch, "E29.26.4", {"start": v(-71.74, -133.13) * mm, "mid": v(-69.4, -132.55) * mm, "end": v(-67.06, -133.1) * mm});
            skArc(sketch, "E29.26.5", {"start": v(-63.85, -137.08) * mm, "mid": v(-64.79, -134.86) * mm, "end": v(-66.63, -133.3) * mm});
            skArc(sketch, "E29.26.6", {"start": v(-63.8, -141.02) * mm, "mid": v(-63.67, -139.05) * mm, "end": v(-63.85, -137.08) * mm});
            skLineSegment(sketch, "E29.26.7", {"start": v(-63.8, -141.02) * mm, "end": v(-63.93, -142.09) * mm});
            skLineSegment(sketch, "E29.26.8", {"start": v(-67.06, -133.1) * mm, "end": v(-66.85, -133.2) * mm});
            skLineSegment(sketch, "E29.26.9", {"start": v(-66.63, -133.3) * mm, "end": v(-66.85, -133.2) * mm});
            skArc(sketch, "E29.27.0", {"start": v(-48.99, -147.9) * mm, "mid": v(-48.86, -149.4) * mm, "end": v(-48.4, -150.83) * mm});
            skArc(sketch, "E29.27.1", {"start": v(-61.3, -143.27) * mm, "mid": v(-62.37, -144.3) * mm, "end": v(-63.66, -145.08) * mm});
            skLineSegment(sketch, "E29.27.2", {"start": v(-60.6, -142.44) * mm, "end": v(-61.3, -143.27) * mm});
            skArc(sketch, "E29.27.3", {"start": v(-60.6, -142.44) * mm, "mid": v(-59.24, -141.01) * mm, "end": v(-57.67, -139.8) * mm});
            skArc(sketch, "E29.27.4", {"start": v(-57.67, -139.8) * mm, "mid": v(-55.4, -138.99) * mm, "end": v(-53.02, -139.29) * mm});
            skArc(sketch, "E29.27.5", {"start": v(-49.42, -142.92) * mm, "mid": v(-50.58, -140.8) * mm, "end": v(-52.57, -139.45) * mm});
            skArc(sketch, "E29.27.6", {"start": v(-48.95, -146.83) * mm, "mid": v(-49.04, -144.86) * mm, "end": v(-49.42, -142.92) * mm});
            skLineSegment(sketch, "E29.27.7", {"start": v(-48.95, -146.83) * mm, "end": v(-48.99, -147.9) * mm});
            skLineSegment(sketch, "E29.27.8", {"start": v(-53.02, -139.29) * mm, "end": v(-52.8, -139.37) * mm});
            skLineSegment(sketch, "E29.27.9", {"start": v(-52.57, -139.45) * mm, "end": v(-52.8, -139.37) * mm});
            skArc(sketch, "E29.28.0", {"start": v(-33.52, -152.16) * mm, "mid": v(-33.24, -153.64) * mm, "end": v(-32.64, -155.01) * mm});
            skArc(sketch, "E29.28.1", {"start": v(-46.24, -148.81) * mm, "mid": v(-47.2, -149.96) * mm, "end": v(-48.4, -150.86) * mm});
            skLineSegment(sketch, "E29.28.2", {"start": v(-45.64, -147.92) * mm, "end": v(-46.24, -148.81) * mm});
            skArc(sketch, "E29.28.3", {"start": v(-45.64, -147.92) * mm, "mid": v(-44.42, -146.36) * mm, "end": v(-43, -145) * mm});
            skArc(sketch, "E29.28.4", {"start": v(-43, -145) * mm, "mid": v(-40.82, -143.95) * mm, "end": v(-38.42, -144) * mm});
            skArc(sketch, "E29.28.5", {"start": v(-34.46, -147.24) * mm, "mid": v(-35.83, -145.26) * mm, "end": v(-37.95, -144.12) * mm});
            skArc(sketch, "E29.28.6", {"start": v(-33.6, -151.09) * mm, "mid": v(-33.89, -149.13) * mm, "end": v(-34.46, -147.24) * mm});
            skLineSegment(sketch, "E29.28.7", {"start": v(-33.6, -151.09) * mm, "end": v(-33.52, -152.16) * mm});
            skLineSegment(sketch, "E29.28.8", {"start": v(-38.42, -144) * mm, "end": v(-38.19, -144.06) * mm});
            skLineSegment(sketch, "E29.28.9", {"start": v(-37.95, -144.12) * mm, "end": v(-38.19, -144.06) * mm});
            skArc(sketch, "E29.29.0", {"start": v(-17.7, -154.8) * mm, "mid": v(-17.27, -156.24) * mm, "end": v(-16.52, -157.54) * mm});
            skArc(sketch, "E29.29.1", {"start": v(-30.7, -152.78) * mm, "mid": v(-31.54, -154.02) * mm, "end": v(-32.64, -155.03) * mm});
            skLineSegment(sketch, "E29.29.2", {"start": v(-30.19, -151.83) * mm, "end": v(-30.7, -152.78) * mm});
            skArc(sketch, "E29.29.3", {"start": v(-30.19, -151.83) * mm, "mid": v(-29.14, -150.15) * mm, "end": v(-27.85, -148.65) * mm});
            skArc(sketch, "E29.29.4", {"start": v(-27.85, -148.65) * mm, "mid": v(-25.8, -147.38) * mm, "end": v(-23.4, -147.19) * mm});
            skArc(sketch, "E29.29.5", {"start": v(-19.14, -150) * mm, "mid": v(-20.7, -148.18) * mm, "end": v(-22.94, -147.26) * mm});
            skArc(sketch, "E29.29.6", {"start": v(-17.88, -153.74) * mm, "mid": v(-18.37, -151.83) * mm, "end": v(-19.14, -150) * mm});
            skLineSegment(sketch, "E29.29.7", {"start": v(-17.88, -153.74) * mm, "end": v(-17.7, -154.8) * mm});
            skLineSegment(sketch, "E29.29.8", {"start": v(-23.4, -147.19) * mm, "end": v(-23.17, -147.22) * mm});
            skLineSegment(sketch, "E29.29.9", {"start": v(-22.94, -147.26) * mm, "end": v(-23.17, -147.22) * mm});
            skArc(sketch, "E29.30.0", {"start": v(-1.68, -155.8) * mm, "mid": v(-1.11, -157.19) * mm, "end": v(-0.24, -158.4) * mm});
            skArc(sketch, "E29.30.1", {"start": v(-14.82, -155.12) * mm, "mid": v(-15.53, -156.44) * mm, "end": v(-16.53, -157.57) * mm});
            skLineSegment(sketch, "E29.30.2", {"start": v(-14.42, -154.12) * mm, "end": v(-14.82, -155.12) * mm});
            skArc(sketch, "E29.30.3", {"start": v(-14.42, -154.12) * mm, "mid": v(-13.55, -152.35) * mm, "end": v(-12.42, -150.72) * mm});
            skArc(sketch, "E29.30.4", {"start": v(-12.42, -150.72) * mm, "mid": v(-10.51, -149.25) * mm, "end": v(-8.15, -148.81) * mm});
            skArc(sketch, "E29.30.5", {"start": v(-3.62, -151.18) * mm, "mid": v(-5.36, -149.52) * mm, "end": v(-7.67, -148.84) * mm});
            skArc(sketch, "E29.30.6", {"start": v(-1.98, -154.77) * mm, "mid": v(-2.66, -152.9) * mm, "end": v(-3.62, -151.18) * mm});
            skLineSegment(sketch, "E29.30.7", {"start": v(-1.98, -154.77) * mm, "end": v(-1.68, -155.8) * mm});
            skLineSegment(sketch, "E29.30.8", {"start": v(-8.15, -148.81) * mm, "end": v(-7.9, -148.82) * mm});
            skLineSegment(sketch, "E29.30.9", {"start": v(-7.67, -148.84) * mm, "end": v(-7.9, -148.82) * mm});
            skArc(sketch, "E29.31.0", {"start": v(14.34, -155.15) * mm, "mid": v(15.06, -156.47) * mm, "end": v(16.05, -157.6) * mm});
            skArc(sketch, "E29.31.1", {"start": v(1.2, -155.82) * mm, "mid": v(0.64, -157.21) * mm, "end": v(-0.24, -158.43) * mm});
            skLineSegment(sketch, "E29.31.2", {"start": v(1.5, -154.8) * mm, "end": v(1.2, -155.82) * mm});
            skArc(sketch, "E29.31.3", {"start": v(1.5, -154.8) * mm, "mid": v(2.19, -152.93) * mm, "end": v(3.14, -151.2) * mm});
            skArc(sketch, "E29.31.4", {"start": v(3.14, -151.2) * mm, "mid": v(4.89, -149.54) * mm, "end": v(7.2, -148.86) * mm});
            skArc(sketch, "E29.31.5", {"start": v(11.95, -150.75) * mm, "mid": v(10.04, -149.28) * mm, "end": v(7.67, -148.84) * mm});
            skArc(sketch, "E29.31.6", {"start": v(13.94, -154.15) * mm, "mid": v(13.07, -152.37) * mm, "end": v(11.95, -150.75) * mm});
            skLineSegment(sketch, "E29.31.7", {"start": v(13.94, -154.15) * mm, "end": v(14.34, -155.15) * mm});
            skLineSegment(sketch, "E29.31.8", {"start": v(7.2, -148.86) * mm, "end": v(7.43, -148.85) * mm});
            skLineSegment(sketch, "E29.31.9", {"start": v(7.67, -148.84) * mm, "end": v(7.43, -148.85) * mm});
            skArc(sketch, "E29.32.0", {"start": v(30.22, -152.85) * mm, "mid": v(31.07, -154.1) * mm, "end": v(32.17, -155.1) * mm});
            skArc(sketch, "E29.32.1", {"start": v(17.22, -154.87) * mm, "mid": v(16.8, -156.31) * mm, "end": v(16.05, -157.62) * mm});
            skLineSegment(sketch, "E29.32.2", {"start": v(17.41, -153.82) * mm, "end": v(17.22, -154.87) * mm});
            skArc(sketch, "E29.32.3", {"start": v(17.41, -153.82) * mm, "mid": v(17.9, -151.9) * mm, "end": v(18.67, -150.08) * mm});
            skArc(sketch, "E29.32.4", {"start": v(18.67, -150.08) * mm, "mid": v(20.24, -148.25) * mm, "end": v(22.46, -147.33) * mm});
            skArc(sketch, "E29.32.5", {"start": v(27.38, -148.72) * mm, "mid": v(25.33, -147.45) * mm, "end": v(22.94, -147.26) * mm});
            skArc(sketch, "E29.32.6", {"start": v(29.72, -151.9) * mm, "mid": v(28.67, -150.22) * mm, "end": v(27.38, -148.72) * mm});
            skLineSegment(sketch, "E29.32.7", {"start": v(29.72, -151.9) * mm, "end": v(30.22, -152.85) * mm});
            skLineSegment(sketch, "E29.32.8", {"start": v(22.46, -147.33) * mm, "end": v(22.7, -147.3) * mm});
            skLineSegment(sketch, "E29.32.9", {"start": v(22.94, -147.26) * mm, "end": v(22.7, -147.3) * mm});
            skArc(sketch, "E29.33.0", {"start": v(45.78, -148.93) * mm, "mid": v(46.74, -150.08) * mm, "end": v(47.95, -150.98) * mm});
            skArc(sketch, "E29.33.1", {"start": v(33.06, -152.28) * mm, "mid": v(32.78, -153.76) * mm, "end": v(32.18, -155.13) * mm});
            skLineSegment(sketch, "E29.33.2", {"start": v(33.14, -151.2) * mm, "end": v(33.06, -152.28) * mm});
            skArc(sketch, "E29.33.3", {"start": v(33.14, -151.2) * mm, "mid": v(33.43, -149.25) * mm, "end": v(34, -147.36) * mm});
            skArc(sketch, "E29.33.4", {"start": v(34, -147.36) * mm, "mid": v(35.37, -145.38) * mm, "end": v(37.5, -144.24) * mm});
            skArc(sketch, "E29.33.5", {"start": v(42.53, -145.11) * mm, "mid": v(40.36, -144.07) * mm, "end": v(37.95, -144.12) * mm});
            skArc(sketch, "E29.33.6", {"start": v(45.18, -148.04) * mm, "mid": v(43.96, -146.48) * mm, "end": v(42.53, -145.11) * mm});
            skLineSegment(sketch, "E29.33.7", {"start": v(45.18, -148.04) * mm, "end": v(45.78, -148.93) * mm});
            skLineSegment(sketch, "E29.33.8", {"start": v(37.5, -144.24) * mm, "end": v(37.72, -144.18) * mm});
            skLineSegment(sketch, "E29.33.9", {"start": v(37.95, -144.12) * mm, "end": v(37.72, -144.18) * mm});
            skArc(sketch, "E29.34.0", {"start": v(60.85, -143.44) * mm, "mid": v(61.93, -144.48) * mm, "end": v(63.22, -145.25) * mm});
            skArc(sketch, "E29.34.1", {"start": v(48.54, -148.08) * mm, "mid": v(48.42, -149.57) * mm, "end": v(47.96, -151) * mm});
            skLineSegment(sketch, "E29.34.2", {"start": v(48.5, -147) * mm, "end": v(48.54, -148.08) * mm});
            skArc(sketch, "E29.34.3", {"start": v(48.5, -147) * mm, "mid": v(48.6, -145.02) * mm, "end": v(48.97, -143.08) * mm});
            skArc(sketch, "E29.34.4", {"start": v(48.97, -143.08) * mm, "mid": v(50.13, -140.97) * mm, "end": v(52.13, -139.62) * mm});
            skArc(sketch, "E29.34.5", {"start": v(57.23, -139.97) * mm, "mid": v(54.96, -139.15) * mm, "end": v(52.57, -139.45) * mm});
            skArc(sketch, "E29.34.6", {"start": v(60.16, -142.6) * mm, "mid": v(58.8, -141.18) * mm, "end": v(57.23, -139.97) * mm});
            skLineSegment(sketch, "E29.34.7", {"start": v(60.16, -142.6) * mm, "end": v(60.85, -143.44) * mm});
            skLineSegment(sketch, "E29.34.8", {"start": v(52.13, -139.62) * mm, "end": v(52.35, -139.54) * mm});
            skLineSegment(sketch, "E29.34.9", {"start": v(52.57, -139.45) * mm, "end": v(52.35, -139.54) * mm});
            skArc(sketch, "E29.35.0", {"start": v(75.27, -136.42) * mm, "mid": v(76.46, -137.34) * mm, "end": v(77.82, -137.98) * mm});
            skArc(sketch, "E29.35.1", {"start": v(63.5, -142.3) * mm, "mid": v(63.54, -143.8) * mm, "end": v(63.23, -145.27) * mm});
            skLineSegment(sketch, "E29.35.2", {"start": v(63.37, -141.23) * mm, "end": v(63.5, -142.3) * mm});
            skArc(sketch, "E29.35.3", {"start": v(63.37, -141.23) * mm, "mid": v(63.25, -139.26) * mm, "end": v(63.43, -137.29) * mm});
            skArc(sketch, "E29.35.4", {"start": v(63.43, -137.29) * mm, "mid": v(64.36, -135.07) * mm, "end": v(66.2, -133.52) * mm});
            skArc(sketch, "E29.35.5", {"start": v(71.31, -133.35) * mm, "mid": v(68.98, -132.77) * mm, "end": v(66.63, -133.3) * mm});
            skArc(sketch, "E29.35.6", {"start": v(74.5, -135.67) * mm, "mid": v(73, -134.39) * mm, "end": v(71.31, -133.35) * mm});
            skLineSegment(sketch, "E29.35.7", {"start": v(74.5, -135.67) * mm, "end": v(75.27, -136.42) * mm});
            skLineSegment(sketch, "E29.35.8", {"start": v(66.2, -133.52) * mm, "end": v(66.42, -133.42) * mm});
            skLineSegment(sketch, "E29.35.9", {"start": v(66.63, -133.3) * mm, "end": v(66.42, -133.42) * mm});
            skArc(sketch, "E29.36.0", {"start": v(88.9, -127.96) * mm, "mid": v(90.17, -128.76) * mm, "end": v(91.6, -129.24) * mm});
            skArc(sketch, "E29.36.1", {"start": v(77.8, -135.02) * mm, "mid": v(77.99, -136.5) * mm, "end": v(77.83, -138) * mm});
            skLineSegment(sketch, "E29.36.2", {"start": v(77.55, -133.97) * mm, "end": v(77.8, -135.02) * mm});
            skArc(sketch, "E29.36.3", {"start": v(77.55, -133.97) * mm, "mid": v(77.23, -132.02) * mm, "end": v(77.2, -130.04) * mm});
            skArc(sketch, "E29.36.4", {"start": v(77.2, -130.04) * mm, "mid": v(77.91, -127.74) * mm, "end": v(79.58, -126) * mm});
            skArc(sketch, "E29.36.5", {"start": v(84.65, -125.3) * mm, "mid": v(82.26, -124.97) * mm, "end": v(79.99, -125.75) * mm});
            skArc(sketch, "E29.36.6", {"start": v(88.06, -127.29) * mm, "mid": v(86.43, -126.17) * mm, "end": v(84.65, -125.3) * mm});
            skLineSegment(sketch, "E29.36.7", {"start": v(88.06, -127.29) * mm, "end": v(88.9, -127.96) * mm});
            skLineSegment(sketch, "E29.36.8", {"start": v(79.58, -126) * mm, "end": v(79.79, -125.88) * mm});
            skLineSegment(sketch, "E29.36.9", {"start": v(79.99, -125.75) * mm, "end": v(79.79, -125.88) * mm});
            skArc(sketch, "E29.37.0", {"start": v(101.59, -118.14) * mm, "mid": v(102.93, -118.8) * mm, "end": v(104.4, -119.14) * mm});
            skArc(sketch, "E29.37.1", {"start": v(91.27, -126.3) * mm, "mid": v(91.6, -127.76) * mm, "end": v(91.6, -129.26) * mm});
            skLineSegment(sketch, "E29.37.2", {"start": v(90.92, -125.29) * mm, "end": v(91.27, -126.3) * mm});
            skArc(sketch, "E29.37.3", {"start": v(90.92, -125.29) * mm, "mid": v(90.4, -123.38) * mm, "end": v(90.17, -121.41) * mm});
            skArc(sketch, "E29.37.4", {"start": v(90.17, -121.41) * mm, "mid": v(90.63, -119.05) * mm, "end": v(92.12, -117.16) * mm});
            skArc(sketch, "E29.37.5", {"start": v(97.08, -115.94) * mm, "mid": v(94.68, -115.85) * mm, "end": v(92.5, -116.86) * mm});
            skArc(sketch, "E29.37.6", {"start": v(100.68, -117.56) * mm, "mid": v(98.94, -116.61) * mm, "end": v(97.08, -115.94) * mm});
            skLineSegment(sketch, "E29.37.7", {"start": v(100.68, -117.56) * mm, "end": v(101.59, -118.14) * mm});
            skLineSegment(sketch, "E29.37.8", {"start": v(92.12, -117.16) * mm, "end": v(92.3, -117) * mm});
            skLineSegment(sketch, "E29.37.9", {"start": v(92.5, -116.86) * mm, "end": v(92.3, -117) * mm});
            skArc(sketch, "E29.38.0", {"start": v(113.2, -107.07) * mm, "mid": v(114.6, -107.59) * mm, "end": v(116.1, -107.78) * mm});
            skArc(sketch, "E29.38.1", {"start": v(103.78, -116.25) * mm, "mid": v(104.26, -117.67) * mm, "end": v(104.41, -119.16) * mm});
            skLineSegment(sketch, "E29.38.2", {"start": v(103.32, -115.27) * mm, "end": v(103.78, -116.25) * mm});
            skArc(sketch, "E29.38.3", {"start": v(103.32, -115.27) * mm, "mid": v(102.6, -113.43) * mm, "end": v(102.17, -111.5) * mm});
            skArc(sketch, "E29.38.4", {"start": v(102.17, -111.5) * mm, "mid": v(102.4, -109.1) * mm, "end": v(103.68, -107.06) * mm});
            skArc(sketch, "E29.38.5", {"start": v(108.49, -105.34) * mm, "mid": v(106.09, -105.5) * mm, "end": v(104.02, -106.73) * mm});
            skArc(sketch, "E29.38.6", {"start": v(112.24, -106.58) * mm, "mid": v(110.4, -105.82) * mm, "end": v(108.49, -105.34) * mm});
            skLineSegment(sketch, "E29.38.7", {"start": v(112.24, -106.58) * mm, "end": v(113.2, -107.07) * mm});
            skLineSegment(sketch, "E29.38.8", {"start": v(103.68, -107.06) * mm, "end": v(103.85, -106.9) * mm});
            skLineSegment(sketch, "E29.38.9", {"start": v(104.02, -106.73) * mm, "end": v(103.85, -106.9) * mm});
            skArc(sketch, "E29.39.0", {"start": v(123.6, -94.86) * mm, "mid": v(125.06, -95.23) * mm, "end": v(126.56, -95.27) * mm});
            skArc(sketch, "E29.39.1", {"start": v(115.18, -104.96) * mm, "mid": v(115.8, -106.32) * mm, "end": v(116.11, -107.8) * mm});
            skLineSegment(sketch, "E29.39.2", {"start": v(114.62, -104.04) * mm, "end": v(115.18, -104.96) * mm});
            skArc(sketch, "E29.39.3", {"start": v(114.62, -104.04) * mm, "mid": v(113.72, -102.28) * mm, "end": v(113.1, -100.4) * mm});
            skArc(sketch, "E29.39.4", {"start": v(113.1, -100.4) * mm, "mid": v(113.07, -98) * mm, "end": v(114.14, -95.84) * mm});
            skArc(sketch, "E29.39.5", {"start": v(118.75, -93.63) * mm, "mid": v(116.37, -94.03) * mm, "end": v(114.44, -95.47) * mm});
            skArc(sketch, "E29.39.6", {"start": v(122.6, -94.48) * mm, "mid": v(120.7, -93.9) * mm, "end": v(118.75, -93.63) * mm});
            skLineSegment(sketch, "E29.39.7", {"start": v(122.6, -94.48) * mm, "end": v(123.6, -94.86) * mm});
            skLineSegment(sketch, "E29.39.8", {"start": v(114.14, -95.84) * mm, "end": v(114.29, -95.65) * mm});
            skLineSegment(sketch, "E29.39.9", {"start": v(114.44, -95.47) * mm, "end": v(114.29, -95.65) * mm});
            skArc(sketch, "E29.40.0", {"start": v(132.7, -81.65) * mm, "mid": v(134.19, -81.87) * mm, "end": v(135.68, -81.75) * mm});
            skArc(sketch, "E29.40.1", {"start": v(125.36, -92.56) * mm, "mid": v(126.12, -93.85) * mm, "end": v(126.58, -95.28) * mm});
            skLineSegment(sketch, "E29.40.2", {"start": v(124.71, -91.7) * mm, "end": v(125.36, -92.56) * mm});
            skArc(sketch, "E29.40.3", {"start": v(124.71, -91.7) * mm, "mid": v(123.64, -90.04) * mm, "end": v(122.82, -88.24) * mm});
            skArc(sketch, "E29.40.4", {"start": v(122.82, -88.24) * mm, "mid": v(122.54, -85.85) * mm, "end": v(123.39, -83.6) * mm});
            skArc(sketch, "E29.40.5", {"start": v(127.74, -80.92) * mm, "mid": v(125.42, -81.57) * mm, "end": v(123.65, -83.2) * mm});
            skArc(sketch, "E29.40.6", {"start": v(131.66, -81.37) * mm, "mid": v(129.72, -81) * mm, "end": v(127.74, -80.92) * mm});
            skLineSegment(sketch, "E29.40.7", {"start": v(131.66, -81.37) * mm, "end": v(132.7, -81.65) * mm});
            skLineSegment(sketch, "E29.40.8", {"start": v(123.39, -83.6) * mm, "end": v(123.52, -83.4) * mm});
            skLineSegment(sketch, "E29.40.9", {"start": v(123.65, -83.2) * mm, "end": v(123.52, -83.4) * mm});
            skArc(sketch, "E29.41.0", {"start": v(140.4, -67.57) * mm, "mid": v(141.9, -67.64) * mm, "end": v(143.37, -67.37) * mm});
            skArc(sketch, "E29.41.1", {"start": v(134.21, -79.18) * mm, "mid": v(135.1, -80.39) * mm, "end": v(135.7, -81.76) * mm});
            skLineSegment(sketch, "E29.41.2", {"start": v(133.48, -78.4) * mm, "end": v(134.21, -79.18) * mm});
            skArc(sketch, "E29.41.3", {"start": v(133.48, -78.4) * mm, "mid": v(132.24, -76.85) * mm, "end": v(131.24, -75.14) * mm});
            skArc(sketch, "E29.41.4", {"start": v(131.24, -75.14) * mm, "mid": v(130.72, -72.8) * mm, "end": v(131.33, -70.46) * mm});
            skArc(sketch, "E29.41.5", {"start": v(135.39, -67.36) * mm, "mid": v(133.15, -68.24) * mm, "end": v(131.55, -70.04) * mm});
            skArc(sketch, "E29.41.6", {"start": v(139.33, -67.4) * mm, "mid": v(137.36, -67.23) * mm, "end": v(135.39, -67.36) * mm});
            skLineSegment(sketch, "E29.41.7", {"start": v(139.33, -67.4) * mm, "end": v(140.4, -67.57) * mm});
            skLineSegment(sketch, "E29.41.8", {"start": v(131.33, -70.46) * mm, "end": v(131.44, -70.25) * mm});
            skLineSegment(sketch, "E29.41.9", {"start": v(131.55, -70.04) * mm, "end": v(131.44, -70.25) * mm});
            skArc(sketch, "E29.42.0", {"start": v(146.6, -52.78) * mm, "mid": v(148.1, -52.7) * mm, "end": v(149.54, -52.27) * mm});
            skArc(sketch, "E29.42.1", {"start": v(141.64, -64.96) * mm, "mid": v(142.66, -66.07) * mm, "end": v(143.4, -67.38) * mm});
            skLineSegment(sketch, "E29.42.2", {"start": v(140.83, -64.25) * mm, "end": v(141.64, -64.96) * mm});
            skArc(sketch, "E29.42.3", {"start": v(140.83, -64.25) * mm, "mid": v(139.44, -62.85) * mm, "end": v(138.27, -61.25) * mm});
            skArc(sketch, "E29.42.4", {"start": v(138.27, -61.25) * mm, "mid": v(137.51, -58.97) * mm, "end": v(137.88, -56.59) * mm});
            skArc(sketch, "E29.42.5", {"start": v(141.6, -53.08) * mm, "mid": v(139.46, -54.19) * mm, "end": v(138.05, -56.15) * mm});
            skArc(sketch, "E29.42.6", {"start": v(145.52, -52.72) * mm, "mid": v(143.55, -52.75) * mm, "end": v(141.6, -53.08) * mm});
            skLineSegment(sketch, "E29.42.7", {"start": v(145.52, -52.72) * mm, "end": v(146.6, -52.78) * mm});
            skLineSegment(sketch, "E29.42.8", {"start": v(137.88, -56.59) * mm, "end": v(137.96, -56.37) * mm});
            skLineSegment(sketch, "E29.42.9", {"start": v(138.05, -56.15) * mm, "end": v(137.96, -56.37) * mm});
            skArc(sketch, "E29.43.0", {"start": v(151.25, -37.42) * mm, "mid": v(152.73, -37.18) * mm, "end": v(154.12, -36.62) * mm});
            skArc(sketch, "E29.43.1", {"start": v(147.57, -50.05) * mm, "mid": v(148.7, -51.05) * mm, "end": v(149.56, -52.28) * mm});
            skLineSegment(sketch, "E29.43.2", {"start": v(146.7, -49.43) * mm, "end": v(147.57, -50.05) * mm});
            skArc(sketch, "E29.43.3", {"start": v(146.7, -49.43) * mm, "mid": v(145.16, -48.18) * mm, "end": v(143.84, -46.7) * mm});
            skArc(sketch, "E29.43.4", {"start": v(143.84, -46.7) * mm, "mid": v(142.85, -44.51) * mm, "end": v(142.96, -42.11) * mm});
            skArc(sketch, "E29.43.5", {"start": v(146.3, -38.24) * mm, "mid": v(144.29, -39.56) * mm, "end": v(143.1, -41.65) * mm});
            skArc(sketch, "E29.43.6", {"start": v(150.17, -37.47) * mm, "mid": v(148.2, -37.71) * mm, "end": v(146.3, -38.24) * mm});
            skLineSegment(sketch, "E29.43.7", {"start": v(150.17, -37.47) * mm, "end": v(151.25, -37.42) * mm});
            skLineSegment(sketch, "E29.43.8", {"start": v(142.96, -42.11) * mm, "end": v(143.03, -41.88) * mm});
            skLineSegment(sketch, "E29.43.9", {"start": v(143.1, -41.65) * mm, "end": v(143.03, -41.88) * mm});
            skArc(sketch, "E29.44.0", {"start": v(154.3, -21.68) * mm, "mid": v(155.74, -21.28) * mm, "end": v(157.07, -20.58) * mm});
            skArc(sketch, "E29.44.1", {"start": v(151.94, -34.61) * mm, "mid": v(153.15, -35.5) * mm, "end": v(154.14, -36.62) * mm});
            skLineSegment(sketch, "E29.44.2", {"start": v(151, -34.09) * mm, "end": v(151.94, -34.61) * mm});
            skArc(sketch, "E29.44.3", {"start": v(151, -34.09) * mm, "mid": v(149.35, -33) * mm, "end": v(147.88, -31.67) * mm});
            skArc(sketch, "E29.44.4", {"start": v(147.88, -31.67) * mm, "mid": v(146.67, -29.6) * mm, "end": v(146.53, -27.19) * mm});
            skArc(sketch, "E29.44.5", {"start": v(149.46, -23) * mm, "mid": v(147.6, -24.52) * mm, "end": v(146.62, -26.72) * mm});
            skArc(sketch, "E29.44.6", {"start": v(153.23, -21.84) * mm, "mid": v(151.3, -22.28) * mm, "end": v(149.46, -23) * mm});
            skLineSegment(sketch, "E29.44.7", {"start": v(153.23, -21.84) * mm, "end": v(154.3, -21.68) * mm});
            skLineSegment(sketch, "E29.44.8", {"start": v(146.53, -27.19) * mm, "end": v(146.58, -26.95) * mm});
            skLineSegment(sketch, "E29.44.9", {"start": v(146.62, -26.72) * mm, "end": v(146.58, -26.95) * mm});
            skArc(sketch, "E29.45.0", {"start": v(155.7, -5.7) * mm, "mid": v(157.1, -5.16) * mm, "end": v(158.35, -4.32) * mm});
            skArc(sketch, "E29.45.1", {"start": v(154.69, -18.8) * mm, "mid": v(156, -19.56) * mm, "end": v(157.1, -20.58) * mm});
            skLineSegment(sketch, "E29.45.2", {"start": v(153.7, -18.38) * mm, "end": v(154.69, -18.8) * mm});
            skArc(sketch, "E29.45.3", {"start": v(153.7, -18.38) * mm, "mid": v(151.95, -17.47) * mm, "end": v(150.35, -16.3) * mm});
            skArc(sketch, "E29.45.4", {"start": v(150.35, -16.3) * mm, "mid": v(148.93, -14.35) * mm, "end": v(148.55, -11.98) * mm});
            skArc(sketch, "E29.45.5", {"start": v(151.03, -7.5) * mm, "mid": v(149.33, -9.21) * mm, "end": v(148.6, -11.5) * mm});
            skArc(sketch, "E29.45.6", {"start": v(154.66, -5.96) * mm, "mid": v(152.8, -6.6) * mm, "end": v(151.03, -7.5) * mm});
            skLineSegment(sketch, "E29.45.7", {"start": v(154.66, -5.96) * mm, "end": v(155.7, -5.7) * mm});
            skLineSegment(sketch, "E29.45.8", {"start": v(148.55, -11.98) * mm, "end": v(148.57, -11.74) * mm});
            skLineSegment(sketch, "E29.45.9", {"start": v(148.6, -11.5) * mm, "end": v(148.57, -11.74) * mm});
            skArc(sketch, "E29.46.0", {"start": v(155.46, 10.34) * mm, "mid": v(156.8, 11.02) * mm, "end": v(157.95, 11.99) * mm});
            skArc(sketch, "E29.46.1", {"start": v(155.8, -2.8) * mm, "mid": v(157.18, -3.41) * mm, "end": v(158.37, -4.32) * mm});
            skLineSegment(sketch, "E29.46.2", {"start": v(154.78, -2.48) * mm, "end": v(155.8, -2.8) * mm});
            skArc(sketch, "E29.46.3", {"start": v(154.78, -2.48) * mm, "mid": v(152.94, -1.75) * mm, "end": v(151.23, -0.75) * mm});
            skArc(sketch, "E29.46.4", {"start": v(151.23, -0.75) * mm, "mid": v(149.62, 1.04) * mm, "end": v(149, 3.36) * mm});
            skArc(sketch, "E29.46.5", {"start": v(151, 8.06) * mm, "mid": v(149.49, 6.2) * mm, "end": v(148.99, 3.84) * mm});
            skArc(sketch, "E29.46.6", {"start": v(154.46, 9.97) * mm, "mid": v(152.66, 9.14) * mm, "end": v(151, 8.06) * mm});
            skLineSegment(sketch, "E29.46.7", {"start": v(154.46, 9.97) * mm, "end": v(155.46, 10.34) * mm});
            skLineSegment(sketch, "E29.46.8", {"start": v(149, 3.36) * mm, "end": v(149, 3.6) * mm});
            skLineSegment(sketch, "E29.46.9", {"start": v(148.99, 3.84) * mm, "end": v(149, 3.6) * mm});
            skArc(sketch, "E29.47.0", {"start": v(153.58, 26.27) * mm, "mid": v(154.84, 27.09) * mm, "end": v(155.88, 28.17) * mm});
            skArc(sketch, "E29.47.1", {"start": v(155.27, 13.23) * mm, "mid": v(156.7, 12.77) * mm, "end": v(157.98, 12) * mm});
            skLineSegment(sketch, "E29.47.2", {"start": v(154.21, 13.45) * mm, "end": v(155.27, 13.23) * mm});
            skArc(sketch, "E29.47.3", {"start": v(154.21, 13.45) * mm, "mid": v(152.3, 13.98) * mm, "end": v(150.5, 14.8) * mm});
            skArc(sketch, "E29.47.4", {"start": v(150.5, 14.8) * mm, "mid": v(148.72, 16.41) * mm, "end": v(147.86, 18.66) * mm});
            skArc(sketch, "E29.47.5", {"start": v(149.37, 23.55) * mm, "mid": v(148.06, 21.53) * mm, "end": v(147.8, 19.14) * mm});
            skArc(sketch, "E29.47.6", {"start": v(152.61, 25.8) * mm, "mid": v(150.9, 24.8) * mm, "end": v(149.37, 23.55) * mm});
            skLineSegment(sketch, "E29.47.7", {"start": v(152.61, 25.8) * mm, "end": v(153.58, 26.27) * mm});
            skLineSegment(sketch, "E29.47.8", {"start": v(147.86, 18.66) * mm, "end": v(147.83, 18.9) * mm});
            skLineSegment(sketch, "E29.47.9", {"start": v(147.8, 19.14) * mm, "end": v(147.83, 18.9) * mm});
            skArc(sketch, "E29.48.0", {"start": v(150.06, 41.93) * mm, "mid": v(151.23, 42.87) * mm, "end": v(152.16, 44.04) * mm});
            skArc(sketch, "E29.48.1", {"start": v(153.08, 29.13) * mm, "mid": v(154.55, 28.8) * mm, "end": v(155.9, 28.17) * mm});
            skLineSegment(sketch, "E29.48.2", {"start": v(152.01, 29.23) * mm, "end": v(153.08, 29.13) * mm});
            skArc(sketch, "E29.48.3", {"start": v(152.01, 29.23) * mm, "mid": v(150.06, 29.57) * mm, "end": v(148.19, 30.2) * mm});
            skArc(sketch, "E29.48.4", {"start": v(148.19, 30.2) * mm, "mid": v(146.24, 31.62) * mm, "end": v(145.16, 33.77) * mm});
            skArc(sketch, "E29.48.5", {"start": v(146.16, 38.78) * mm, "mid": v(145.06, 36.64) * mm, "end": v(145.05, 34.23) * mm});
            skArc(sketch, "E29.48.6", {"start": v(149.15, 41.35) * mm, "mid": v(147.56, 40.18) * mm, "end": v(146.16, 38.78) * mm});
            skLineSegment(sketch, "E29.48.7", {"start": v(149.15, 41.35) * mm, "end": v(150.06, 41.93) * mm});
            skLineSegment(sketch, "E29.48.8", {"start": v(145.16, 33.77) * mm, "end": v(145.1, 34) * mm});
            skLineSegment(sketch, "E29.48.9", {"start": v(145.05, 34.23) * mm, "end": v(145.1, 34) * mm});
            skArc(sketch, "E29.49.0", {"start": v(144.96, 57.13) * mm, "mid": v(146.02, 58.19) * mm, "end": v(146.83, 59.46) * mm});
            skArc(sketch, "E29.49.1", {"start": v(149.28, 44.71) * mm, "mid": v(150.77, 44.55) * mm, "end": v(152.19, 44.05) * mm});
            skLineSegment(sketch, "E29.49.2", {"start": v(148.2, 44.7) * mm, "end": v(149.28, 44.71) * mm});
            skArc(sketch, "E29.49.3", {"start": v(148.2, 44.7) * mm, "mid": v(146.23, 44.84) * mm, "end": v(144.3, 45.27) * mm});
            skArc(sketch, "E29.49.4", {"start": v(144.3, 45.27) * mm, "mid": v(142.22, 46.49) * mm, "end": v(140.92, 48.51) * mm});
            skArc(sketch, "E29.49.5", {"start": v(141.4, 53.6) * mm, "mid": v(140.52, 51.36) * mm, "end": v(140.76, 48.96) * mm});
            skArc(sketch, "E29.49.6", {"start": v(144.1, 56.47) * mm, "mid": v(142.65, 55.14) * mm, "end": v(141.4, 53.6) * mm});
            skLineSegment(sketch, "E29.49.7", {"start": v(144.1, 56.47) * mm, "end": v(144.96, 57.13) * mm});
            skLineSegment(sketch, "E29.49.8", {"start": v(140.92, 48.51) * mm, "end": v(140.84, 48.74) * mm});
            skLineSegment(sketch, "E29.49.9", {"start": v(140.76, 48.96) * mm, "end": v(140.84, 48.74) * mm});
            skArc(sketch, "E29.50.0", {"start": v(138.31, 71.74) * mm, "mid": v(139.27, 72.9) * mm, "end": v(139.94, 74.24) * mm});
            skArc(sketch, "E29.50.1", {"start": v(143.89, 59.82) * mm, "mid": v(145.39, 59.81) * mm, "end": v(146.85, 59.47) * mm});
            skLineSegment(sketch, "E29.50.2", {"start": v(142.82, 59.7) * mm, "end": v(143.89, 59.82) * mm});
            skArc(sketch, "E29.50.3", {"start": v(142.82, 59.7) * mm, "mid": v(140.84, 59.64) * mm, "end": v(138.88, 59.87) * mm});
            skArc(sketch, "E29.50.4", {"start": v(138.88, 59.87) * mm, "mid": v(136.68, 60.86) * mm, "end": v(135.18, 62.75) * mm});
            skArc(sketch, "E29.50.5", {"start": v(135.14, 67.86) * mm, "mid": v(134.5, 65.54) * mm, "end": v(134.98, 63.18) * mm});
            skArc(sketch, "E29.50.6", {"start": v(137.54, 70.99) * mm, "mid": v(136.22, 69.51) * mm, "end": v(135.14, 67.86) * mm});
            skLineSegment(sketch, "E29.50.7", {"start": v(137.54, 70.99) * mm, "end": v(138.31, 71.74) * mm});
            skLineSegment(sketch, "E29.50.8", {"start": v(135.18, 62.75) * mm, "end": v(135.08, 62.96) * mm});
            skLineSegment(sketch, "E29.50.9", {"start": v(134.98, 63.18) * mm, "end": v(135.08, 62.96) * mm});
            skArc(sketch, "E29.51.0", {"start": v(130.2, 85.58) * mm, "mid": v(131.03, 86.83) * mm, "end": v(131.56, 88.23) * mm});
            skArc(sketch, "E29.51.1", {"start": v(136.97, 74.3) * mm, "mid": v(138.47, 74.45) * mm, "end": v(139.96, 74.25) * mm});
            skLineSegment(sketch, "E29.51.2", {"start": v(135.92, 74.08) * mm, "end": v(136.97, 74.3) * mm});
            skArc(sketch, "E29.51.3", {"start": v(135.92, 74.08) * mm, "mid": v(133.96, 73.8) * mm, "end": v(131.98, 73.83) * mm});
            skArc(sketch, "E29.51.4", {"start": v(131.98, 73.83) * mm, "mid": v(129.7, 74.6) * mm, "end": v(128.01, 76.31) * mm});
            skArc(sketch, "E29.51.5", {"start": v(127.45, 81.4) * mm, "mid": v(127.05, 79.02) * mm, "end": v(127.77, 76.72) * mm});
            skArc(sketch, "E29.51.6", {"start": v(129.51, 84.75) * mm, "mid": v(128.35, 83.15) * mm, "end": v(127.45, 81.4) * mm});
            skLineSegment(sketch, "E29.51.7", {"start": v(129.51, 84.75) * mm, "end": v(130.2, 85.58) * mm});
            skLineSegment(sketch, "E29.51.8", {"start": v(128.01, 76.31) * mm, "end": v(127.9, 76.52) * mm});
            skLineSegment(sketch, "E29.51.9", {"start": v(127.77, 76.72) * mm, "end": v(127.9, 76.52) * mm});
            skArc(sketch, "E29.52.0", {"start": v(120.71, 98.51) * mm, "mid": v(121.41, 99.84) * mm, "end": v(121.8, 101.3) * mm});
            skArc(sketch, "E29.52.1", {"start": v(128.6, 88) * mm, "mid": v(130.08, 88.29) * mm, "end": v(131.58, 88.25) * mm});
            skLineSegment(sketch, "E29.52.2", {"start": v(127.59, 87.66) * mm, "end": v(128.6, 88) * mm});
            skArc(sketch, "E29.52.3", {"start": v(127.59, 87.66) * mm, "mid": v(125.66, 87.2) * mm, "end": v(123.7, 87.01) * mm});
            skArc(sketch, "E29.52.4", {"start": v(123.7, 87.01) * mm, "mid": v(121.34, 87.54) * mm, "end": v(119.49, 89.07) * mm});
            skArc(sketch, "E29.52.5", {"start": v(118.4, 94.07) * mm, "mid": v(118.25, 91.66) * mm, "end": v(119.2, 89.45) * mm});
            skArc(sketch, "E29.52.6", {"start": v(120.11, 97.62) * mm, "mid": v(119.12, 95.9) * mm, "end": v(118.4, 94.07) * mm});
            skLineSegment(sketch, "E29.52.7", {"start": v(120.11, 97.62) * mm, "end": v(120.71, 98.51) * mm});
            skLineSegment(sketch, "E29.52.8", {"start": v(119.49, 89.07) * mm, "end": v(119.35, 89.26) * mm});
            skLineSegment(sketch, "E29.52.9", {"start": v(119.2, 89.45) * mm, "end": v(119.35, 89.26) * mm});
            skArc(sketch, "E29.53.0", {"start": v(109.95, 110.4) * mm, "mid": v(110.5, 111.8) * mm, "end": v(110.73, 113.28) * mm});
            skArc(sketch, "E29.53.1", {"start": v(118.88, 100.75) * mm, "mid": v(120.31, 101.2) * mm, "end": v(121.8, 101.3) * mm});
            skLineSegment(sketch, "E29.53.2", {"start": v(117.9, 100.31) * mm, "end": v(118.88, 100.75) * mm});
            skArc(sketch, "E29.53.3", {"start": v(117.9, 100.31) * mm, "mid": v(116.03, 99.65) * mm, "end": v(114.1, 99.27) * mm});
            skArc(sketch, "E29.53.4", {"start": v(114.1, 99.27) * mm, "mid": v(111.7, 99.55) * mm, "end": v(109.7, 100.89) * mm});
            skArc(sketch, "E29.53.5", {"start": v(108.1, 105.74) * mm, "mid": v(108.2, 103.34) * mm, "end": v(109.37, 101.24) * mm});
            skArc(sketch, "E29.53.6", {"start": v(109.44, 109.45) * mm, "mid": v(108.63, 107.65) * mm, "end": v(108.1, 105.74) * mm});
            skLineSegment(sketch, "E29.53.7", {"start": v(109.44, 109.45) * mm, "end": v(109.95, 110.4) * mm});
            skLineSegment(sketch, "E29.53.8", {"start": v(109.7, 100.89) * mm, "end": v(109.54, 101.06) * mm});
            skLineSegment(sketch, "E29.53.9", {"start": v(109.37, 101.24) * mm, "end": v(109.54, 101.06) * mm});
            skArc(sketch, "E29.54.0", {"start": v(98.01, 121.12) * mm, "mid": v(98.42, 122.56) * mm, "end": v(98.5, 124.06) * mm});
            skArc(sketch, "E29.54.1", {"start": v(107.9, 112.44) * mm, "mid": v(109.27, 113.03) * mm, "end": v(110.75, 113.3) * mm});
            skLineSegment(sketch, "E29.54.2", {"start": v(106.96, 111.9) * mm, "end": v(107.9, 112.44) * mm});
            skArc(sketch, "E29.54.3", {"start": v(106.96, 111.9) * mm, "mid": v(105.17, 111.05) * mm, "end": v(103.28, 110.47) * mm});
            skArc(sketch, "E29.54.4", {"start": v(103.28, 110.47) * mm, "mid": v(100.87, 110.5) * mm, "end": v(98.74, 111.63) * mm});
            skArc(sketch, "E29.54.5", {"start": v(96.66, 116.3) * mm, "mid": v(97, 113.91) * mm, "end": v(98.39, 111.94) * mm});
            skArc(sketch, "E29.54.6", {"start": v(97.6, 120.13) * mm, "mid": v(96.99, 118.25) * mm, "end": v(96.66, 116.3) * mm});
            skLineSegment(sketch, "E29.54.7", {"start": v(97.6, 120.13) * mm, "end": v(98.01, 121.12) * mm});
            skLineSegment(sketch, "E29.54.8", {"start": v(98.74, 111.63) * mm, "end": v(98.56, 111.79) * mm});
            skLineSegment(sketch, "E29.54.9", {"start": v(98.39, 111.94) * mm, "end": v(98.56, 111.79) * mm});
            skArc(sketch, "E29.55.0", {"start": v(85.04, 130.56) * mm, "mid": v(85.3, 132.03) * mm, "end": v(85.22, 133.53) * mm});
            skArc(sketch, "E29.55.1", {"start": v(95.76, 122.94) * mm, "mid": v(97.07, 123.67) * mm, "end": v(98.51, 124.08) * mm});
            skLineSegment(sketch, "E29.55.2", {"start": v(94.88, 122.3) * mm, "end": v(95.76, 122.94) * mm});
            skArc(sketch, "E29.55.3", {"start": v(94.88, 122.3) * mm, "mid": v(93.2, 121.28) * mm, "end": v(91.37, 120.5) * mm});
            skArc(sketch, "E29.55.4", {"start": v(91.37, 120.5) * mm, "mid": v(88.98, 120.3) * mm, "end": v(86.74, 121.2) * mm});
            skArc(sketch, "E29.55.5", {"start": v(84.19, 125.62) * mm, "mid": v(84.77, 123.28) * mm, "end": v(86.35, 121.47) * mm});
            skArc(sketch, "E29.55.6", {"start": v(84.73, 129.52) * mm, "mid": v(84.31, 127.6) * mm, "end": v(84.19, 125.62) * mm});
            skLineSegment(sketch, "E29.55.7", {"start": v(84.73, 129.52) * mm, "end": v(85.04, 130.56) * mm});
            skLineSegment(sketch, "E29.55.8", {"start": v(86.74, 121.2) * mm, "end": v(86.55, 121.33) * mm});
            skLineSegment(sketch, "E29.55.9", {"start": v(86.35, 121.47) * mm, "end": v(86.55, 121.33) * mm});
            skArc(sketch, "E29.56.0", {"start": v(71.16, 138.6) * mm, "mid": v(71.27, 140.1) * mm, "end": v(71.04, 141.59) * mm});
            skArc(sketch, "E29.56.1", {"start": v(82.6, 132.13) * mm, "mid": v(83.84, 133) * mm, "end": v(85.23, 133.55) * mm});
            skLineSegment(sketch, "E29.56.2", {"start": v(81.8, 131.42) * mm, "end": v(82.6, 132.13) * mm});
            skArc(sketch, "E29.56.3", {"start": v(81.8, 131.42) * mm, "mid": v(80.23, 130.22) * mm, "end": v(78.5, 129.26) * mm});
            skArc(sketch, "E29.56.4", {"start": v(78.5, 129.26) * mm, "mid": v(76.14, 128.8) * mm, "end": v(73.82, 129.47) * mm});
            skArc(sketch, "E29.56.5", {"start": v(70.82, 133.6) * mm, "mid": v(71.65, 131.35) * mm, "end": v(73.4, 129.7) * mm});
            skArc(sketch, "E29.56.6", {"start": v(70.97, 137.55) * mm, "mid": v(70.75, 135.58) * mm, "end": v(70.82, 133.6) * mm});
            skLineSegment(sketch, "E29.56.7", {"start": v(70.97, 137.55) * mm, "end": v(71.16, 138.6) * mm});
            skLineSegment(sketch, "E29.56.8", {"start": v(73.82, 129.47) * mm, "end": v(73.61, 129.59) * mm});
            skLineSegment(sketch, "E29.56.9", {"start": v(73.4, 129.7) * mm, "end": v(73.61, 129.59) * mm});
            skArc(sketch, "E29.57.0", {"start": v(56.53, 145.19) * mm, "mid": v(56.49, 146.7) * mm, "end": v(56.1, 148.14) * mm});
            skArc(sketch, "E29.57.1", {"start": v(68.59, 139.92) * mm, "mid": v(69.72, 140.9) * mm, "end": v(71.05, 141.6) * mm});
            skLineSegment(sketch, "E29.57.2", {"start": v(67.86, 139.13) * mm, "end": v(68.59, 139.92) * mm});
            skArc(sketch, "E29.57.3", {"start": v(67.86, 139.13) * mm, "mid": v(66.42, 137.78) * mm, "end": v(64.8, 136.65) * mm});
            skArc(sketch, "E29.57.4", {"start": v(64.8, 136.65) * mm, "mid": v(62.49, 135.95) * mm, "end": v(60.12, 136.37) * mm});
            skArc(sketch, "E29.57.5", {"start": v(56.71, 140.18) * mm, "mid": v(57.76, 138.02) * mm, "end": v(59.68, 136.56) * mm});
            skArc(sketch, "E29.57.6", {"start": v(56.45, 144.12) * mm, "mid": v(56.43, 142.14) * mm, "end": v(56.71, 140.18) * mm});
            skLineSegment(sketch, "E29.57.7", {"start": v(56.45, 144.12) * mm, "end": v(56.53, 145.19) * mm});
            skLineSegment(sketch, "E29.57.8", {"start": v(60.12, 136.37) * mm, "end": v(59.9, 136.47) * mm});
            skLineSegment(sketch, "E29.57.9", {"start": v(59.68, 136.56) * mm, "end": v(59.9, 136.47) * mm});
            skArc(sketch, "E29.58.0", {"start": v(41.3, 150.23) * mm, "mid": v(41.1, 151.72) * mm, "end": v(40.57, 153.12) * mm});
            skArc(sketch, "E29.58.1", {"start": v(53.84, 146.23) * mm, "mid": v(54.86, 147.33) * mm, "end": v(56.1, 148.16) * mm});
            skLineSegment(sketch, "E29.58.2", {"start": v(53.2, 145.37) * mm, "end": v(53.84, 146.23) * mm});
            skArc(sketch, "E29.58.3", {"start": v(53.2, 145.37) * mm, "mid": v(51.9, 143.87) * mm, "end": v(50.4, 142.59) * mm});
            skArc(sketch, "E29.58.4", {"start": v(50.4, 142.59) * mm, "mid": v(48.18, 141.65) * mm, "end": v(45.78, 141.83) * mm});
            skArc(sketch, "E29.58.5", {"start": v(42, 145.27) * mm, "mid": v(43.26, 143.22) * mm, "end": v(45.32, 141.98) * mm});
            skArc(sketch, "E29.58.6", {"start": v(41.33, 149.16) * mm, "mid": v(41.52, 147.19) * mm, "end": v(42, 145.27) * mm});
            skLineSegment(sketch, "E29.58.7", {"start": v(41.33, 149.16) * mm, "end": v(41.3, 150.23) * mm});
            skLineSegment(sketch, "E29.58.8", {"start": v(45.78, 141.83) * mm, "end": v(45.55, 141.9) * mm});
            skLineSegment(sketch, "E29.58.9", {"start": v(45.32, 141.98) * mm, "end": v(45.55, 141.9) * mm});
            skArc(sketch, "E29.59.0", {"start": v(25.64, 153.68) * mm, "mid": v(25.29, 155.14) * mm, "end": v(24.61, 156.48) * mm});
            skArc(sketch, "E29.59.1", {"start": v(38.51, 151) * mm, "mid": v(39.42, 152.19) * mm, "end": v(40.58, 153.15) * mm});
            skLineSegment(sketch, "E29.59.2", {"start": v(37.97, 150.07) * mm, "end": v(38.51, 151) * mm});
            skArc(sketch, "E29.59.3", {"start": v(37.97, 150.07) * mm, "mid": v(36.83, 148.45) * mm, "end": v(35.47, 147.01) * mm});
            skArc(sketch, "E29.59.4", {"start": v(35.47, 147.01) * mm, "mid": v(33.36, 145.86) * mm, "end": v(30.95, 145.79) * mm});
            skArc(sketch, "E29.59.5", {"start": v(26.84, 148.82) * mm, "mid": v(28.3, 146.91) * mm, "end": v(30.49, 145.88) * mm});
            skArc(sketch, "E29.59.6", {"start": v(25.77, 152.62) * mm, "mid": v(26.16, 150.68) * mm, "end": v(26.84, 148.82) * mm});
            skLineSegment(sketch, "E29.59.7", {"start": v(25.77, 152.62) * mm, "end": v(25.64, 153.68) * mm});
            skLineSegment(sketch, "E29.59.8", {"start": v(30.95, 145.79) * mm, "end": v(30.72, 145.83) * mm});
            skLineSegment(sketch, "E29.59.9", {"start": v(30.49, 145.88) * mm, "end": v(30.72, 145.83) * mm});
            skArc(sketch, "E29.60.0", {"start": v(9.7, 155.5) * mm, "mid": v(9.2, 156.92) * mm, "end": v(8.4, 158.19) * mm});
            skArc(sketch, "E29.60.1", {"start": v(22.78, 154.15) * mm, "mid": v(23.57, 155.44) * mm, "end": v(24.62, 156.5) * mm});
            skLineSegment(sketch, "E29.60.2", {"start": v(22.33, 153.18) * mm, "end": v(22.78, 154.15) * mm});
            skArc(sketch, "E29.60.3", {"start": v(22.33, 153.18) * mm, "mid": v(21.37, 151.45) * mm, "end": v(20.17, 149.88) * mm});
            skArc(sketch, "E29.60.4", {"start": v(20.17, 149.88) * mm, "mid": v(18.18, 148.51) * mm, "end": v(15.8, 148.2) * mm});
            skArc(sketch, "E29.60.5", {"start": v(11.4, 150.79) * mm, "mid": v(13.05, 149.04) * mm, "end": v(15.32, 148.24) * mm});
            skArc(sketch, "E29.60.6", {"start": v(9.94, 154.46) * mm, "mid": v(10.53, 152.57) * mm, "end": v(11.4, 150.79) * mm});
            skLineSegment(sketch, "E29.60.7", {"start": v(9.94, 154.46) * mm, "end": v(9.7, 155.5) * mm});
            skLineSegment(sketch, "E29.60.8", {"start": v(15.8, 148.2) * mm, "end": v(15.56, 148.22) * mm});
            skLineSegment(sketch, "E29.60.9", {"start": v(15.32, 148.24) * mm, "end": v(15.56, 148.22) * mm});
            skPoint(sketch, "E29.center", {"position": v(0, 0) * mm});
            skSolve(sketch);
        }
        {
            var Q0;
            {var subQ171=sQuery(id+"F2.wireOp",EDGE,"E15");Q0=makeQuery(id+"F2.imprint","IMPRINT",FACE,{"disambiguationData":[TD([[makeQuery(id+"F2.imprint","IMPRINT",EDGE,{"derivedFrom":subQ171}),1.0]])]});}
            extrude(context, id + "F3", {"entities" : qUnion([Q0]), "operationType" : NewBodyOperationType.INTERSECT, "endBound" : BoundingType.THROUGH_ALL, "oppositeDirection" : true, "depth" : 25 * mm, "offsetDistance" : 25 * mm});
        }
        {
            var Q0;
            Q0=qCreatedBy(makeId("Right.planeOp"),FACE);
            var sketch = newSketch(context, id + "F4", { "sketchPlane" : qUnion([Q0])});
            skLineSegment(sketch, "E30", {"start": v(0, 72.2) * mm, "end": v(0, -78.72) * mm, "construction": true});
            skLineSegment(sketch, "E31", {"start": v(-84.45, 0) * mm, "end": v(97.88, 0) * mm, "construction": true});
            skCircle(sketch, "E32", {"center": v(0, 0) * mm, "radius": 52 * mm, "construction": true});
            skCircle(sketch, "E33", {"center": v(0, 52) * mm, "radius": 5.25 * mm});
            skCircle(sketch, "E34.1.0", {"center": v(-45.03, 26) * mm, "radius": 5.25 * mm});
            skCircle(sketch, "E34.2.0", {"center": v(-45.03, -26) * mm, "radius": 5.25 * mm});
            skCircle(sketch, "E34.3.0", {"center": v(0, -52) * mm, "radius": 5.25 * mm});
            skCircle(sketch, "E34.4.0", {"center": v(45.03, -26) * mm, "radius": 5.25 * mm});
            skCircle(sketch, "E34.5.0", {"center": v(45.03, 26) * mm, "radius": 5.25 * mm});
            skSolve(sketch);
        }
        {
            var Q0;
            Q0=makeQuery(id+"F4.imprint","IMPRINT",FACE,{"disambiguationData":[TD([[makeQuery(id+"F4.imprint","IMPRINT",EDGE,{"derivedFrom":sQuery(id+"F4.wireOp",EDGE,"E34.5.0")}),1.0]])]});
            var Q1;
            Q1=makeQuery(id+"F4.imprint","IMPRINT",FACE,{"disambiguationData":[TD([[makeQuery(id+"F4.imprint","IMPRINT",EDGE,{"derivedFrom":sQuery(id+"F4.wireOp",EDGE,"E33")}),1.0]])]});
            var Q2;
            Q2=makeQuery(id+"F4.imprint","IMPRINT",FACE,{"disambiguationData":[TD([[makeQuery(id+"F4.imprint","IMPRINT",EDGE,{"derivedFrom":sQuery(id+"F4.wireOp",EDGE,"E34.4.0")}),1.0]])]});
            var Q3;
            Q3=makeQuery(id+"F4.imprint","IMPRINT",FACE,{"disambiguationData":[TD([[makeQuery(id+"F4.imprint","IMPRINT",EDGE,{"derivedFrom":sQuery(id+"F4.wireOp",EDGE,"E34.3.0")}),1.0]])]});
            var Q4;
            Q4=makeQuery(id+"F4.imprint","IMPRINT",FACE,{"disambiguationData":[TD([[makeQuery(id+"F4.imprint","IMPRINT",EDGE,{"derivedFrom":sQuery(id+"F4.wireOp",EDGE,"E34.2.0")}),1.0]])]});
            var Q5;
            Q5=makeQuery(id+"F4.imprint","IMPRINT",FACE,{"disambiguationData":[TD([[makeQuery(id+"F4.imprint","IMPRINT",EDGE,{"derivedFrom":sQuery(id+"F4.wireOp",EDGE,"E34.1.0")}),1.0]])]});
            var Q6;
            Q6=sQuery(id+"F4.wireOp",EDGE,"E34.1.0");
            var Q7;
            Q7=sQuery(id+"F4.wireOp",EDGE,"E33");
            var Q8;
            Q8=sQuery(id+"F4.wireOp",EDGE,"E34.5.0");
            var Q9;
            Q9=sQuery(id+"F4.wireOp",EDGE,"E34.4.0");
            var Q10;
            Q10=sQuery(id+"F4.wireOp",EDGE,"E34.3.0");
            var Q11;
            Q11=sQuery(id+"F4.wireOp",EDGE,"E34.2.0");
            extrude(context, id + "F5", {"entities" : qUnion([Q0, Q1, Q2, Q3, Q4, Q5]), "operationType" : NewBodyOperationType.REMOVE, "surfaceEntities" : qUnion([Q6, Q7, Q8, Q9, Q10, Q11]), "depth" : 25 * mm, "offsetDistance" : 25 * mm});
        }
    });
